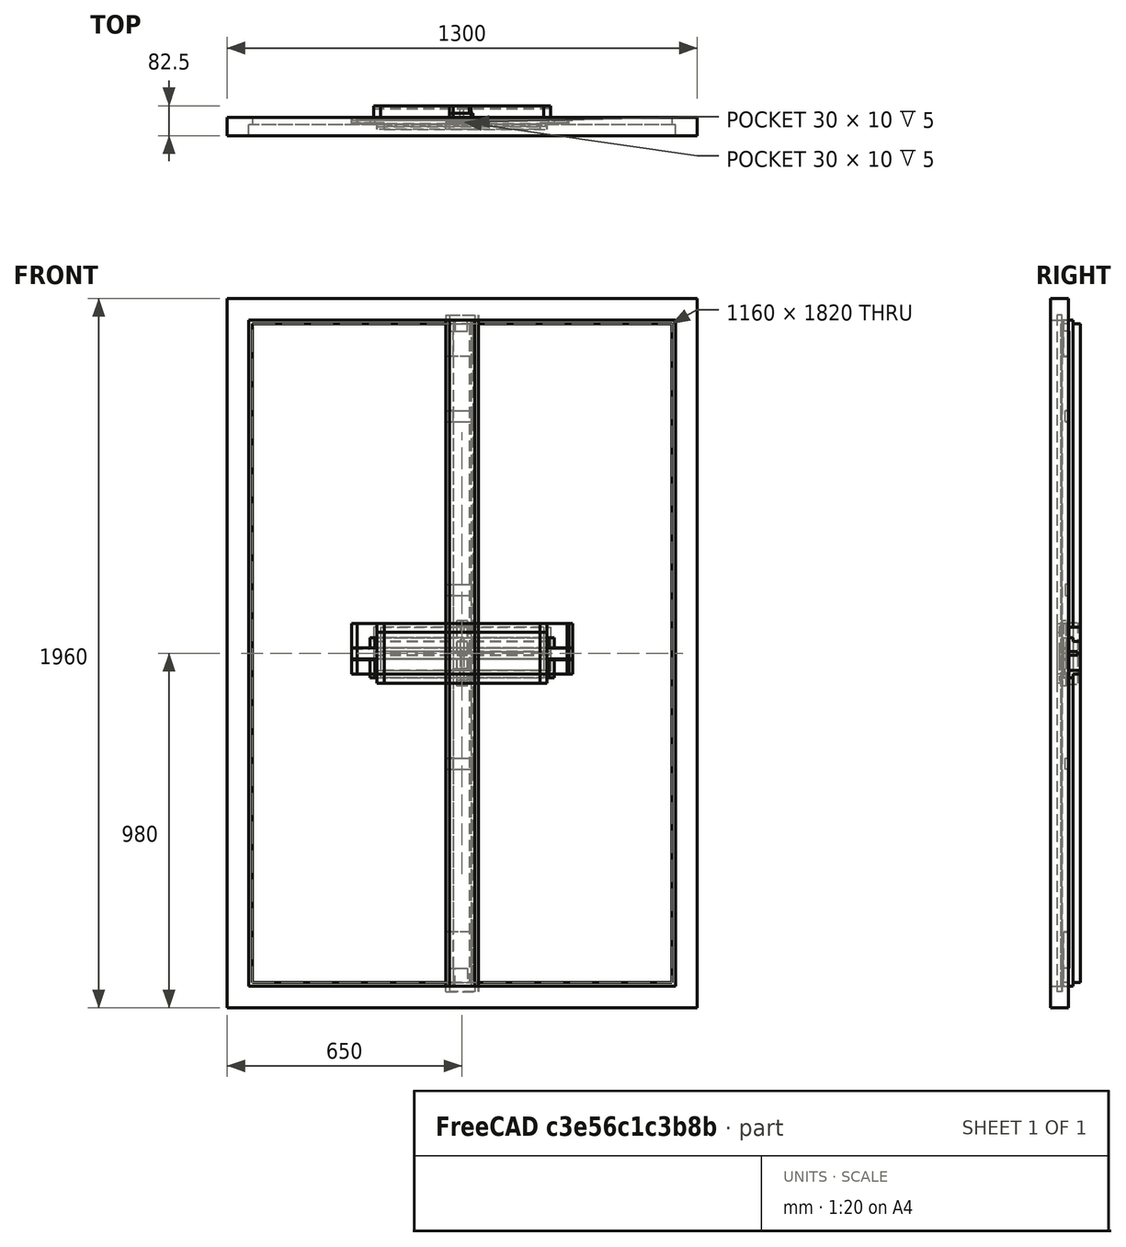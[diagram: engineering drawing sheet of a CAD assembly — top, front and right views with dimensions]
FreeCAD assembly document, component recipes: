
FREECAD ASSEMBLY — COMPONENT RECIPES ("F4.0")

This assembly document has 17 components, labeled P0..P16 below (a component is one placed body or linked part). 17 of them carry a construction recipe — the FreeCAD feature program that regenerates the part from scratch, quoted from this document or its linked companion documents; the rest are supplied as boundary geometry only. No exploded tour is included for this assembly.
COMPONENT P0 — recipe-attached ("Frame002", modeled in this document).
Construction recipe (the document's own serialized feature program — sketch geometry with constraints, then the solid features built on it; lengths are millimeters unless a unit is written):

FEATURE [Sketcher::SketchObject] Sketch064  label="FrameSketch"
  ArcFitTolerance = 0
  AttachmentSupport = -> [XZ_Plane013]
  FullyConstrained = true
  MakeInternals = false
  MapMode = 5
  Placement = pos=(0,0,0) rot=(1,0,0;1.5708rad)
  expr: .Constraints.OpeningHeigth = <<Parameters>>.StileLength - <<Parameters>>.WindowFrameRebateDepth * 2
  expr: .Constraints.OpeningWidth = <<Parameters>>.RailLength * 2 - <<Parameters>>.WindowFrameRebateDepth * 2 - <<Parameters>>.IntersectionRebateDepth
  expr: Constraints[22] = .Constraints.OpeningHeigth + 70 mm * 2
  expr: Constraints[23] = .Constraints.OpeningWidth + 70 mm * 2
  sketch-geometry (10):
    g0: LineSegment StartX=-650 StartY=980 StartZ=0 EndX=-650 EndY=-980 EndZ=0
    g1: LineSegment StartX=-650 StartY=-980 StartZ=0 EndX=650 EndY=-980 EndZ=0
    g2: LineSegment StartX=650 StartY=-980 StartZ=0 EndX=650 EndY=980 EndZ=0
    g3: LineSegment StartX=650 StartY=980 StartZ=0 EndX=-650 EndY=980 EndZ=0
    g4: GeomPoint [constr] X=2.96e-14 Y=2.2e-15 Z=0
    g5: LineSegment StartX=-580 StartY=910 StartZ=0 EndX=-580 EndY=-910 EndZ=0
    g6: LineSegment StartX=-580 StartY=-910 StartZ=0 EndX=580 EndY=-910 EndZ=0
    g7: LineSegment StartX=580 StartY=-910 StartZ=0 EndX=580 EndY=910 EndZ=0
    g8: LineSegment StartX=580 StartY=910 StartZ=0 EndX=-580 EndY=910 EndZ=0
    g9: GeomPoint [constr] X=2.96e-14 Y=2.2e-15 Z=0
  constraints (24):
    c: Coincident(g0,g1)
    c: Coincident(g1,g2)
    c: Coincident(g2,g3)
    c: Coincident(g3,g0)
    c: Vertical(g0)
    c: Vertical(g2)
    c: Horizontal(g1)
    c: Horizontal(g3)
    c: Symmetric(g2,g0,g4)
    c: Coincident(g4,g-1)
    c: Coincident(g5,g6)
    c: Coincident(g6,g7)
    c: Coincident(g7,g8)
    c: Coincident(g8,g5)
    c: Vertical(g5)
    c: Vertical(g7)
    c: Horizontal(g6)
    c: Horizontal(g8)
    c: Symmetric(g7,g5,g9)
    c: Coincident(g9,g4)
    c: DistanceY(g5,g5) = 1820  'OpeningHeigth'
    c: DistanceX(g6,g6) = 1160  'OpeningWidth'
    c: DistanceY(g0,g0) = 1960
    c: DistanceX(g1,g1) = 1300
FEATURE [PartDesign::Pad] Pad006  label="Frame001"
  Direction = (0,-1,2e-16)
  Length = 50
  Length2 = 10
  Placement = pos=(0,0,0) rot=(1,0,0;1.5708rad)
  Profile = -> Sketch064
  ReferenceAxis = -> Sketch064 [N_Axis]
  Refine = true
  Suppressed = false
  Type = 0
  expr: Length = <<Parameters>>.FrameThickness
FEATURE [Sketcher::SketchObject] Sketch065
  ArcFitTolerance = 0
  AttachmentSupport = -> [Pad006]
  FullyConstrained = true
  MakeInternals = false
  MapMode = 5
  Placement = pos=(0,-50,0) rot=(1,0,0;1.5708rad)
  expr: Constraints[10] = <<FrameSketch>>.Constraints.OpeningWidth + 2 * <<Parameters>>.IntersectionRebateDepth
  expr: Constraints[11] = <<FrameSketch>>.Constraints.OpeningHeigth + 2 * <<Parameters>>.IntersectionRebateDepth
  sketch-geometry (5):
    g0: LineSegment StartX=-590 StartY=920 StartZ=0 EndX=-590 EndY=-920 EndZ=0
    g1: LineSegment StartX=-590 StartY=-920 StartZ=0 EndX=590 EndY=-920 EndZ=0
    g2: LineSegment StartX=590 StartY=-920 StartZ=0 EndX=590 EndY=920 EndZ=0
    g3: LineSegment StartX=590 StartY=920 StartZ=0 EndX=-590 EndY=920 EndZ=0
    g4: GeomPoint [constr] X=0 Y=0 Z=0
  constraints (12):
    c: Coincident(g0,g1)
    c: Coincident(g1,g2)
    c: Coincident(g2,g3)
    c: Coincident(g3,g0)
    c: Vertical(g0)
    c: Vertical(g2)
    c: Horizontal(g1)
    c: Horizontal(g3)
    c: Symmetric(g2,g0,g4)
    c: Coincident(g4,g-1)
    c: DistanceX(g3,g3) = 1180
    c: DistanceY(g0,g0) = 1840
FEATURE [PartDesign::Pocket] Pocket057
  BaseFeature = -> Pad006
  Direction = (0,1,-2e-16)
  Length = 30
  Length2 = 5
  Placement = pos=(0,0,0) rot=(1,0,0;1.5708rad)
  Profile = -> Sketch065
  ReferenceAxis = -> Sketch065 [N_Axis]
  Refine = true
  Suppressed = false
  Type = 0
  expr: Length = <<Parameters>>.FrameThickness - <<Parameters>>.WindowFrameRebateWidth
FEATURE [PartDesign::Body] Body013  label="Frame"
  AllowCompound = false
  Group = -> [Sketch064,Pad006,Sketch065,Pocket057]
  Origin = -> Origin013
  Tip = -> Pocket057
COMPONENT P1 — recipe-attached ("Muntin bar001", modeled in this document).
Construction recipe (the document's own serialized feature program — sketch geometry with constraints, then the solid features built on it; lengths are millimeters unless a unit is written):

FEATURE [PartDesign::Plane] DatumPlane  label="DatumPlane top"
  AttachmentOffset = pos=(0,0,90) rot=(0,0,1;0rad)
  AttachmentSupport = -> [X_Axis]
  Length = 30
  MapMode = 2
  Placement = pos=(0,0,90) rot=(0,0,1;0rad)
  ResizeMode = 1
  Width = 50
  expr: .AttachmentOffset.Base.z = <<Parameters>>.MuntinBarLength / 2
  expr: Length = <<Parameters>>.MuntinWidth
  expr: Width = <<Parameters>>.MuntinThickness
FEATURE [PartDesign::Plane] DatumPlane001  label="DatumPlane right"
  AttachmentOffset = pos=(0,0,15) rot=(0,0,1;0rad)
  AttachmentSupport = -> [X_Axis]
  Length = 50
  MapMode = 4
  Placement = pos=(15,0,0) rot=(0.57735,0.57735,0.57735;2.0944rad)
  ResizeMode = 1
  Width = 180
  expr: .AttachmentOffset.Base.z = <<Parameters>>.MuntinWidth / 2
  expr: Length = <<Parameters>>.MuntinThickness
  expr: Width = <<Parameters>>.MuntinBarLength
FEATURE [PartDesign::Plane] DatumPlane002  label="DatumPlane front"
  AttachmentOffset = pos=(0,0,25) rot=(0,0,1;0rad)
  AttachmentSupport = -> [X_Axis]
  Length = 30
  MapMode = 3
  Placement = pos=(0,-25,5.6e-15) rot=(1,0,0;1.5708rad)
  ResizeMode = 1
  Width = 180
  expr: .AttachmentOffset.Base.z = <<Parameters>>.MuntinThickness / 2
  expr: Length = <<Parameters>>.MuntinWidth
  expr: Width = <<Parameters>>.MuntinBarLength
FEATURE [Sketcher::SketchObject] Sketch
  ArcFitTolerance = 0
  AttachmentSupport = -> [DatumPlane]
  FullyConstrained = true
  MakeInternals = false
  MapMode = 5
  Placement = pos=(0,0,90) rot=(0,0,1;0rad)
  expr: Constraints[10] = <<Parameters>>.MuntinWidth
  expr: Constraints[11] = <<Parameters>>.MuntinThickness
  sketch-geometry (5):
    g0: LineSegment StartX=-15 StartY=25 StartZ=0 EndX=-15 EndY=-25 EndZ=0
    g1: LineSegment StartX=-15 StartY=-25 StartZ=0 EndX=15 EndY=-25 EndZ=0
    g2: LineSegment StartX=15 StartY=-25 StartZ=0 EndX=15 EndY=25 EndZ=0
    g3: LineSegment StartX=15 StartY=25 StartZ=0 EndX=-15 EndY=25 EndZ=0
    g4: GeomPoint [constr] X=0 Y=0 Z=0
  constraints (12):
    c: Coincident(g0,g1)
    c: Coincident(g1,g2)
    c: Coincident(g2,g3)
    c: Coincident(g3,g0)
    c: Vertical(g0)
    c: Vertical(g2)
    c: Horizontal(g1)
    c: Horizontal(g3)
    c: Symmetric(g2,g0,g4)
    c: Coincident(g4,g-1)
    c: DistanceX(g3,g3) = 30
    c: DistanceY(g0,g0) = 50
FEATURE [PartDesign::Pad] Pad  label="Stock"
  Direction = (0,0,1)
  Length = 180
  Length2 = 10
  Placement = pos=(0,0,90) rot=(0,0,1;0rad)
  Profile = -> Sketch
  ReferenceAxis = -> Sketch [N_Axis]
  Refine = true
  Reversed = true
  Suppressed = false
  Type = 0
  expr: Length = <<Parameters>>.MuntinBarLength
FEATURE [Sketcher::SketchObject] Sketch001
  ArcFitTolerance = 0
  AttachmentSupport = -> [DatumPlane001]
  ExternalGeometry = -> [DatumPlane,DatumPlane002]
  FullyConstrained = true
  MakeInternals = false
  MapMode = 5
  Placement = pos=(15,0,0) rot=(0.57735,0.57735,0.57735;2.0944rad)
  expr: Constraints[14] = <<Parameters>>.MuntinBarTenonLength
  expr: Constraints[16] = <<Parameters>>.GlassRebateDepth
  expr: Constraints[18] = <<Parameters>>.MuntinThickness
  expr: Constraints[19] = <<Parameters>>.MuntinTenonThickness
  expr: Constraints[20] = <<Parameters>>.MuntinBarTenonLength - <<Parameters>>.GlassRebateWidth
  sketch-geometry (8):
    g0: LineSegment StartX=-17 StartY=90 StartZ=0 EndX=-17 EndY=75 EndZ=0
    g1: LineSegment StartX=-17 StartY=75 StartZ=0 EndX=-25 EndY=75 EndZ=0
    g2: LineSegment StartX=-25 StartY=75 StartZ=0 EndX=-25 EndY=90 EndZ=0
    g3: LineSegment StartX=-25 StartY=90 StartZ=0 EndX=-17 EndY=90 EndZ=0
    g4: LineSegment StartX=-7 StartY=90 StartZ=0 EndX=-7 EndY=85 EndZ=0
    g5: LineSegment StartX=-7 StartY=85 StartZ=0 EndX=25 EndY=85 EndZ=0
    g6: LineSegment StartX=25 StartY=85 StartZ=0 EndX=25 EndY=90 EndZ=0
    g7: LineSegment StartX=25 StartY=90 StartZ=0 EndX=-7 EndY=90 EndZ=0
  constraints (23):
    c: Coincident(g0,g1)
    c: Coincident(g1,g2)
    c: Coincident(g2,g3)
    c: Coincident(g3,g0)
    c: Vertical(g0)
    c: Horizontal(g1)
    c: Coincident(g4,g5)
    c: Coincident(g5,g6)
    c: Coincident(g6,g7)
    c: Coincident(g7,g4)
    c: Vertical(g4)
    c: Vertical(g6)
    c: Horizontal(g5)
    c: Horizontal(g7)
    c: DistanceY(g0,g0) = 15
    c: DistanceX(g1,g1) = -8
    c: DistanceX(g7,g7) = 32
    c: Horizontal(g4,g2)
    c: DistanceX(g2,g6) = 50
    c: DistanceX(g0,g4) = 10
    c: DistanceY(g6,g6) = 5
    c: Tangent(g2,g-4)
    c: Tangent(g3,g-3)
FEATURE [PartDesign::Pocket] Pocket  label="Tenon top"
  BaseFeature = -> Pad
  Direction = (-1,0,0)
  Length = 5
  Length2 = 5
  Placement = pos=(0,0,90) rot=(0,0,1;0rad)
  Profile = -> Sketch001
  ReferenceAxis = -> Sketch001 [N_Axis]
  Refine = true
  Suppressed = false
  Type = 1
FEATURE [PartDesign::Mirrored] Mirrored  label="Tenon bottom"
  BaseFeature = -> Pocket
  MirrorPlane = -> XY_Plane
  Originals = -> [Pocket]
  Placement = pos=(0,0,90) rot=(0,0,1;0rad)
  Refine = true
  Suppressed = false
  TransformMode = 0
FEATURE [Sketcher::SketchObject] Sketch002
  ArcFitTolerance = 0
  AttachmentSupport = -> [DatumPlane]
  ExternalGeometry = -> [DatumPlane001,DatumPlane002]
  FullyConstrained = true
  MakeInternals = false
  MapMode = 5
  Placement = pos=(0,0,90) rot=(0,0,1;0rad)
  expr: Constraints[7] = <<Parameters>>.GlassRebateDepth
  expr: Constraints[8] = <<Parameters>>.GlassRebateWidth
  expr: Constraints[9] = <<Parameters>>.MuntinThickness
  sketch-geometry (4):
    g0: LineSegment StartX=5 StartY=25 StartZ=0 EndX=5 EndY=-7 EndZ=0
    g1: LineSegment StartX=5 StartY=-7 StartZ=0 EndX=15 EndY=-7 EndZ=0
    g2: LineSegment StartX=15 StartY=-7 StartZ=0 EndX=15 EndY=25 EndZ=0
    g3: LineSegment StartX=15 StartY=25 StartZ=0 EndX=5 EndY=25 EndZ=0
  constraints (11):
    c: Coincident(g0,g1)
    c: Coincident(g1,g2)
    c: Coincident(g2,g3)
    c: Coincident(g3,g0)
    c: Vertical(g0)
    c: Horizontal(g1)
    c: Horizontal(g3)
    c: DistanceY(g0,g0) = 32
    c: DistanceX(g3,g3) = 10
    c: Distance(g2,g-4) = 50
    c: Tangent(g2,g-3)
FEATURE [PartDesign::Pocket] Pocket001  label="Glass rebate right"
  BaseFeature = -> Mirrored
  Direction = (0,0,-1)
  Length = 5
  Length2 = 5
  Placement = pos=(0,0,90) rot=(0,0,1;0rad)
  Profile = -> Sketch002
  ReferenceAxis = -> Sketch002 [N_Axis]
  Refine = true
  Suppressed = false
  Type = 1
FEATURE [PartDesign::Mirrored] Mirrored001  label="Glass rebate left"
  BaseFeature = -> Pocket001
  MirrorPlane = -> Sketch002 [V_Axis]
  Originals = -> [Pocket001]
  Placement = pos=(0,0,90) rot=(0,0,1;0rad)
  Refine = true
  Suppressed = false
  TransformMode = 0
FEATURE [PartDesign::Body] Body  label="Muntin bar"
  AllowCompound = false
  Group = -> [DatumPlane,DatumPlane001,DatumPlane002,Sketch,Pad,Sketch001,Pocket,Mirrored,Sketch002,Pocket001,Mirrored001]
  Origin = -> Origin
  Tip = -> Mirrored001
COMPONENT P2 — same part as P1; its construction recipe is shown at P1.
COMPONENT P3 — recipe-attached ("Muntin partitioned left001", modeled in this document).
Construction recipe (the document's own serialized feature program — sketch geometry with constraints, then the solid features built on it; lengths are millimeters unless a unit is written):

FEATURE [PartDesign::FeatureBase] BaseFeature002
  BaseFeature = -> Binder002
  Suppressed = false
FEATURE [PartDesign::Plane] DatumPlane023  label="DatumPlane top005"
  AttachmentOffset = pos=(0,0,15) rot=(0,0,1;0rad)
  AttachmentSupport = -> [X_Axis006]
  Length = 610
  MapMode = 2
  Placement = pos=(0,0,15) rot=(0,0,1;0rad)
  ResizeMode = 1
  Width = 50
  expr: .AttachmentOffset.Base.z = <<Parameters>>.MuntinWidth / 2
  expr: Length = <<Parameters>>.RailLength
  expr: Width = <<Parameters>>.MuntinThickness
FEATURE [PartDesign::Plane] DatumPlane024  label="DatumPlane right004"
  AttachmentOffset = pos=(0,0,305) rot=(0,0,1;0rad)
  AttachmentSupport = -> [X_Axis006]
  Length = 50
  MapMode = 4
  Placement = pos=(305,0,0) rot=(0.57735,0.57735,0.57735;2.0944rad)
  ResizeMode = 1
  Width = 30
  expr: .AttachmentOffset.Base.z = <<Parameters>>.RailLength / 2
  expr: Length = <<Parameters>>.MuntinThickness
  expr: Width = <<Parameters>>.MuntinWidth
FEATURE [PartDesign::Plane] DatumPlane025  label="DatumPlane front003"
  AttachmentOffset = pos=(0,0,25) rot=(0,0,1;0rad)
  AttachmentSupport = -> [X_Axis006]
  Length = 610
  MapMode = 3
  Placement = pos=(0,-25,5.6e-15) rot=(1,0,0;1.5708rad)
  ResizeMode = 1
  Width = 30
  expr: .AttachmentOffset.Base.z = <<Parameters>>.MuntinThickness / 2
  expr: Length = <<Parameters>>.RailLength
  expr: Width = <<Parameters>>.MuntinWidth
FEATURE [PartDesign::Plane] DatumPlane026  label="DatumPlane left004"
  AttachmentOffset = pos=(0,0,305) rot=(0,0,1;0rad)
  AttachmentSupport = -> [X_Axis006]
  Length = 50
  MapMode = 4
  Placement = pos=(-305,0,0) rot=(0.57735,-0.57735,-0.57735;2.0944rad)
  ResizeMode = 1
  Width = 30
  expr: .AttachmentOffset.Base.z = <<Parameters>>.RailLength / 2
  expr: Length = <<Parameters>>.MuntinThickness
  expr: Width = <<Parameters>>.MuntinWidth
FEATURE [PartDesign::Plane] DatumPlane027  label="DatumPlane rear004"
  AttachmentOffset = pos=(0,0,25) rot=(0,0,1;0rad)
  AttachmentSupport = -> [X_Axis006]
  Length = 610
  MapMode = 3
  Placement = pos=(0,25,-5.6e-15) rot=(0,0.707107,0.707107;3.14159rad)
  ResizeMode = 1
  Width = 30
  expr: .AttachmentOffset.Base.z = <<Parameters>>.MuntinThickness / 2
  expr: Length = <<Parameters>>.RailLength
  expr: Width = <<Parameters>>.MuntinWidth
FEATURE [Sketcher::SketchObject] Sketch040
  ArcFitTolerance = 0
  AttachmentSupport = -> [DatumPlane023]
  ExternalGeometry = -> [DatumPlane027,DatumPlane024]
  FullyConstrained = true
  MakeInternals = false
  MapMode = 5
  Placement = pos=(0,0,15) rot=(0,0,1;0rad)
  expr: Constraints[10] = <<Parameters>>.GlassRebateDepth
  expr: Constraints[11] = <<Parameters>>.GlassOpeningWidth / 2 - <<Parameters>>.MuntinWidth / 2 + <<Parameters>>.StileInnerWidth
  expr: Constraints[8] = <<Parameters>>.MuntinTenonThickness
  expr: Constraints[9] = <<Parameters>>.MuntinWidth
  sketch-geometry (4):
    g0: LineSegment StartX=-5 StartY=-7 StartZ=0 EndX=-5 EndY=-17 EndZ=0
    g1: LineSegment StartX=-5 StartY=-17 StartZ=0 EndX=25 EndY=-17 EndZ=0
    g2: LineSegment StartX=25 StartY=-17 StartZ=0 EndX=25 EndY=-7 EndZ=0
    g3: LineSegment StartX=25 StartY=-7 StartZ=0 EndX=-5 EndY=-7 EndZ=0
  constraints (12):
    c: Coincident(g0,g1)
    c: Coincident(g1,g2)
    c: Coincident(g2,g3)
    c: Coincident(g3,g0)
    c: Vertical(g0)
    c: Vertical(g2)
    c: Horizontal(g1)
    c: Horizontal(g3)
    c: DistanceY(g2,g2) = 10
    c: DistanceX(g1,g1) = 30
    c: Distance(g0,g-3) = 32
    c: Distance(g2,g-4) = 280
FEATURE [PartDesign::Pocket] Pocket035  label="Muntin bar mortise"
  BaseFeature = -> BaseFeature002
  Direction = (0,0,-1)
  Length = 15
  Length2 = 5
  Profile = -> Sketch040
  ReferenceAxis = -> Sketch040 [N_Axis]
  Refine = true
  Suppressed = false
  Type = 0
  expr: Length = <<Parameters>>.MuntinBarTenonLength
FEATURE [Sketcher::SketchObject] Sketch041
  ArcFitTolerance = 0
  AttachmentSupport = -> [DatumPlane023]
  ExternalGeometry = -> [DatumPlane024,DatumPlane027]
  FullyConstrained = true
  MakeInternals = false
  MapMode = 5
  Placement = pos=(0,0,15) rot=(0,0,1;0rad)
  expr: Constraints[10] = <<Parameters>>.IntersectionRebateWidth
  expr: Constraints[5] = <<Parameters>>.IntersectionRebateDepth
  expr: Constraints[6] = <<Parameters>>.IntersectionRebateWidth
  sketch-geometry (4):
    g0: LineSegment StartX=295 StartY=-7.5 StartZ=0 EndX=295 EndY=-40 EndZ=0
    g1: LineSegment StartX=295 StartY=-40 StartZ=0 EndX=305 EndY=-40 EndZ=0
    g2: LineSegment StartX=305 StartY=-40 StartZ=0 EndX=305 EndY=-7.5 EndZ=0
    g3: LineSegment StartX=305 StartY=-7.5 StartZ=0 EndX=295 EndY=-7.5 EndZ=0
  constraints (11):
    c: Coincident(g0,g1)
    c: Coincident(g1,g2)
    c: Coincident(g2,g3)
    c: Coincident(g3,g0)
    c: Horizontal(g3)
    c: Distance(g3,g3) = 10
    c: DistanceY(g0,g0) = 32.5
    c: Vertical(g0,g0)
    c: Horizontal(g0,g1)
    c: Tangent(g2,g-3)
    c: Distance(g2,g-4) = 32.5
FEATURE [PartDesign::Pocket] Pocket036  label="Frame inner intersection rebate001"
  BaseFeature = -> Pocket035
  Direction = (0,0,-1)
  Length = 5
  Length2 = 5
  Profile = -> Sketch041
  ReferenceAxis = -> Sketch041 [N_Axis]
  Refine = true
  Suppressed = false
  Type = 1
FEATURE [PartDesign::Body] Body006  label="Muntin partitioned left"
  AllowCompound = false
  Group = -> [DatumPlane023,DatumPlane024,DatumPlane025,DatumPlane026,DatumPlane027,BaseFeature002,Sketch040,Pocket035,Sketch041,Pocket036]
  Origin = -> Origin006
  Tip = -> Pocket036
COMPONENT P4 — recipe-attached ("Muntin partitioned right001", modeled in this document).
Construction recipe (the document's own serialized feature program — sketch geometry with constraints, then the solid features built on it; lengths are millimeters unless a unit is written):

FEATURE [PartDesign::FeatureBase] BaseFeature004
  BaseFeature = -> Part__Mirroring003
  Suppressed = false
FEATURE [PartDesign::Body] Body008  label="Muntin partitioned right"
  AllowCompound = false
  BaseFeature = -> Part__Mirroring003
  Group = -> [BaseFeature004]
  Origin = -> Origin008
  Tip = -> BaseFeature004
COMPONENT P5 — recipe-attached ("Muntin single left001", modeled in this document).
Construction recipe (the document's own serialized feature program — sketch geometry with constraints, then the solid features built on it; lengths are millimeters unless a unit is written):

FEATURE [PartDesign::Plane] DatumPlane018  label="DatumPlane top004"
  AttachmentOffset = pos=(0,0,15) rot=(0,0,1;0rad)
  AttachmentSupport = -> [X_Axis005]
  Length = 610
  MapMode = 2
  Placement = pos=(0,0,15) rot=(0,0,1;0rad)
  ResizeMode = 1
  Width = 50
  expr: .AttachmentOffset.Base.z = <<Parameters>>.MuntinWidth / 2
  expr: Length = <<Parameters>>.RailLength
  expr: Width = <<Parameters>>.MuntinThickness
FEATURE [PartDesign::Plane] DatumPlane019  label="DatumPlane right003"
  AttachmentOffset = pos=(0,0,305) rot=(0,0,1;0rad)
  AttachmentSupport = -> [X_Axis005]
  Length = 50
  MapMode = 4
  Placement = pos=(305,0,0) rot=(0.57735,0.57735,0.57735;2.0944rad)
  ResizeMode = 1
  Width = 30
  expr: .AttachmentOffset.Base.z = <<Parameters>>.RailLength / 2
  expr: Length = <<Parameters>>.MuntinThickness
  expr: Width = <<Parameters>>.MuntinWidth
FEATURE [PartDesign::Plane] DatumPlane020  label="DatumPlane front002"
  AttachmentOffset = pos=(0,0,25) rot=(0,0,1;0rad)
  AttachmentSupport = -> [X_Axis005]
  Length = 610
  MapMode = 3
  Placement = pos=(0,-25,5.6e-15) rot=(1,0,0;1.5708rad)
  ResizeMode = 1
  Width = 30
  expr: .AttachmentOffset.Base.z = <<Parameters>>.MuntinThickness / 2
  expr: Length = <<Parameters>>.RailLength
  expr: Width = <<Parameters>>.MuntinWidth
FEATURE [Sketcher::SketchObject] Sketch033
  ArcFitTolerance = 0
  AttachmentSupport = -> [DatumPlane019]
  FullyConstrained = true
  MakeInternals = false
  MapMode = 5
  Placement = pos=(305,0,0) rot=(0.57735,0.57735,0.57735;2.0944rad)
  expr: Constraints[10] = <<Parameters>>.MuntinThickness
  expr: Constraints[11] = <<Parameters>>.MuntinWidth
  sketch-geometry (5):
    g0: LineSegment StartX=-25 StartY=15 StartZ=0 EndX=-25 EndY=-15 EndZ=0
    g1: LineSegment StartX=-25 StartY=-15 StartZ=0 EndX=25 EndY=-15 EndZ=0
    g2: LineSegment StartX=25 StartY=-15 StartZ=0 EndX=25 EndY=15 EndZ=0
    g3: LineSegment StartX=25 StartY=15 StartZ=0 EndX=-25 EndY=15 EndZ=0
    g4: GeomPoint [constr] X=0 Y=0 Z=0
  constraints (12):
    c: Coincident(g0,g1)
    c: Coincident(g1,g2)
    c: Coincident(g2,g3)
    c: Coincident(g3,g0)
    c: Vertical(g0)
    c: Vertical(g2)
    c: Horizontal(g1)
    c: Horizontal(g3)
    c: Symmetric(g2,g0,g4)
    c: Coincident(g4,g-1)
    c: DistanceX(g3,g3) = 50
    c: DistanceY(g0,g0) = 30
FEATURE [PartDesign::Pad] Pad003  label="Stock003"
  Direction = (1,0,0)
  Length = 610
  Length2 = 10
  Placement = pos=(305,0,0) rot=(0.57735,0.57735,0.57735;2.0944rad)
  Profile = -> Sketch033
  ReferenceAxis = -> Sketch033 [N_Axis]
  Refine = true
  Reversed = true
  Suppressed = false
  Type = 0
  expr: Length = <<Parameters>>.RailLength
FEATURE [Sketcher::SketchObject] Sketch034
  ArcFitTolerance = 0
  AttachmentSupport = -> [DatumPlane018]
  ExternalGeometry = -> [DatumPlane019,DatumPlane020]
  FullyConstrained = true
  MakeInternals = false
  MapMode = 5
  Placement = pos=(0,0,15) rot=(0,0,1;0rad)
  expr: Constraints[14] = <<Parameters>>.StileInnerWidth - <<Parameters>>.GlassRebateWidth
  expr: Constraints[15] = <<Parameters>>.MuntinThickness
  expr: Constraints[16] = <<Parameters>>.GlassRebateDepth
  expr: Constraints[17] = <<Parameters>>.MuntinTenonThickness
  expr: Constraints[18] = <<Parameters>>.StileInnerWidth
  sketch-geometry (8):
    g0: LineSegment StartX=305 StartY=-17 StartZ=0 EndX=235 EndY=-17 EndZ=0
    g1: LineSegment StartX=235 StartY=-17 StartZ=0 EndX=235 EndY=-25 EndZ=0
    g2: LineSegment StartX=235 StartY=-25 StartZ=0 EndX=305 EndY=-25 EndZ=0
    g3: LineSegment StartX=305 StartY=-25 StartZ=0 EndX=305 EndY=-17 EndZ=0
    g4: LineSegment StartX=305 StartY=25 StartZ=0 EndX=245 EndY=25 EndZ=0
    g5: LineSegment StartX=245 StartY=25 StartZ=0 EndX=245 EndY=-7 EndZ=0
    g6: LineSegment StartX=245 StartY=-7 StartZ=0 EndX=305 EndY=-7 EndZ=0
    g7: LineSegment StartX=305 StartY=-7 StartZ=0 EndX=305 EndY=25 EndZ=0
  constraints (22):
    c: Coincident(g0,g1)
    c: Coincident(g1,g2)
    c: Coincident(g2,g3)
    c: Coincident(g3,g0)
    c: Horizontal(g0)
    c: Vertical(g1)
    c: Vertical(g3)
    c: Coincident(g4,g5)
    c: Coincident(g5,g6)
    c: Coincident(g6,g7)
    c: Coincident(g7,g4)
    c: Horizontal(g4)
    c: Horizontal(g6)
    c: Vertical(g5)
    c: DistanceX(g4,g4) = 60
    c: DistanceY(g2,g4) = 50
    c: DistanceY(g7,g7) = 32
    c: DistanceY(g0,g6) = 10
    c: Distance(g2,g2) = 70
    c: Tangent(g7,g-3)
    c: Vertical(g0,g6)
    c: Tangent(g2,g-4)
FEATURE [PartDesign::Pocket] Pocket029  label="Tenon inner"
  BaseFeature = -> Pad003
  Direction = (0,0,-1)
  Length = 5
  Length2 = 5
  Placement = pos=(305,0,0) rot=(0.57735,0.57735,0.57735;2.0944rad)
  Profile = -> Sketch034
  ReferenceAxis = -> Sketch034 [N_Axis]
  Refine = true
  Suppressed = false
  Type = 1
FEATURE [PartDesign::Plane] DatumPlane021  label="DatumPlane left003"
  AttachmentOffset = pos=(0,0,305) rot=(0,0,1;0rad)
  AttachmentSupport = -> [X_Axis005]
  Length = 50
  MapMode = 4
  Placement = pos=(-305,0,0) rot=(0.57735,-0.57735,-0.57735;2.0944rad)
  ResizeMode = 1
  Width = 30
  expr: .AttachmentOffset.Base.z = <<Parameters>>.RailLength / 2
  expr: Length = <<Parameters>>.MuntinThickness
  expr: Width = <<Parameters>>.MuntinWidth
FEATURE [Sketcher::SketchObject] Sketch036
  ArcFitTolerance = 0
  AttachmentSupport = -> [DatumPlane018]
  ExternalGeometry = -> [DatumPlane021,DatumPlane020]
  FullyConstrained = true
  MakeInternals = false
  MapMode = 5
  Placement = pos=(0,0,15) rot=(0,0,1;0rad)
  expr: Constraints[14] = <<Parameters>>.StileOuterWidth
  expr: Constraints[16] = <<Parameters>>.StileOuterWidth - <<Parameters>>.GlassRebateWidth
  expr: Constraints[17] = <<Parameters>>.GlassRebateDepth
  expr: Constraints[18] = <<Parameters>>.MuntinTenonThickness
  expr: Constraints[19] = <<Parameters>>.MuntinThickness
  sketch-geometry (8):
    g0: LineSegment StartX=-305 StartY=25 StartZ=0 EndX=-305 EndY=-7 EndZ=0
    g1: LineSegment StartX=-305 StartY=-7 StartZ=0 EndX=-225 EndY=-7 EndZ=0
    g2: LineSegment StartX=-225 StartY=-7 StartZ=0 EndX=-225 EndY=25 EndZ=0
    g3: LineSegment StartX=-225 StartY=25 StartZ=0 EndX=-305 EndY=25 EndZ=0
    g4: LineSegment StartX=-305 StartY=-17 StartZ=0 EndX=-305 EndY=-25 EndZ=0
    g5: LineSegment StartX=-305 StartY=-25 StartZ=0 EndX=-215 EndY=-25 EndZ=0
    g6: LineSegment StartX=-215 StartY=-25 StartZ=0 EndX=-215 EndY=-17 EndZ=0
    g7: LineSegment StartX=-215 StartY=-17 StartZ=0 EndX=-305 EndY=-17 EndZ=0
  constraints (22):
    c: Coincident(g0,g1)
    c: Coincident(g1,g2)
    c: Coincident(g2,g3)
    c: Coincident(g3,g0)
    c: Vertical(g2)
    c: Horizontal(g1)
    c: Horizontal(g3)
    c: Coincident(g4,g5)
    c: Coincident(g5,g6)
    c: Coincident(g6,g7)
    c: Coincident(g7,g4)
    c: Vertical(g4)
    c: Vertical(g6)
    c: Horizontal(g7)
    c: DistanceX(g5,g5) = 90
    c: Vertical(g4,g0)
    c: DistanceX(g3,g3) = 80
    c: DistanceY(g0,g0) = 32
    c: Distance(g0,g4) = 10
    c: DistanceY(g4,g0) = 50
    c: Tangent(g0,g-3)
    c: Tangent(g5,g-4)
FEATURE [PartDesign::Pocket] Pocket031  label="Tenon outer"
  BaseFeature = -> Pocket029
  Direction = (0,0,-1)
  Length = 5
  Length2 = 5
  Placement = pos=(305,0,0) rot=(0.57735,0.57735,0.57735;2.0944rad)
  Profile = -> Sketch036
  ReferenceAxis = -> Sketch036 [N_Axis]
  Refine = true
  Suppressed = false
  Type = 1
FEATURE [PartDesign::Plane] DatumPlane022  label="DatumPlane rear003"
  AttachmentOffset = pos=(0,0,25) rot=(0,0,1;0rad)
  AttachmentSupport = -> [X_Axis005]
  Length = 610
  MapMode = 3
  Placement = pos=(0,25,-5.6e-15) rot=(0,0.707107,0.707107;3.14159rad)
  ResizeMode = 1
  Width = 30
  expr: .AttachmentOffset.Base.z = <<Parameters>>.MuntinThickness / 2
  expr: Length = <<Parameters>>.RailLength
  expr: Width = <<Parameters>>.MuntinWidth
FEATURE [Sketcher::SketchObject] Sketch037
  ArcFitTolerance = 0
  AttachmentSupport = -> [DatumPlane019]
  ExternalGeometry = -> [DatumPlane018,DatumPlane022]
  FullyConstrained = true
  MakeInternals = false
  MapMode = 5
  Placement = pos=(305,0,0) rot=(0.57735,0.57735,0.57735;2.0944rad)
  expr: Constraints[6] = <<Parameters>>.GlassRebateDepth
  expr: Constraints[7] = <<Parameters>>.GlassRebateWidth
  sketch-geometry (4):
    g0: LineSegment StartX=25 StartY=15 StartZ=0 EndX=-7 EndY=15 EndZ=0
    g1: LineSegment StartX=-7 StartY=15 StartZ=0 EndX=-7 EndY=5 EndZ=0
    g2: LineSegment StartX=-7 StartY=5 StartZ=0 EndX=25 EndY=5 EndZ=0
    g3: LineSegment StartX=25 StartY=5 StartZ=0 EndX=25 EndY=15 EndZ=0
  constraints (10):
    c: Coincident(g0,g1)
    c: Coincident(g1,g2)
    c: Coincident(g2,g3)
    c: Coincident(g3,g0)
    c: Horizontal(g2)
    c: Vertical(g1)
    c: DistanceX(g0,g0) = 32
    c: DistanceY(g3,g3) = 10
    c: Tangent(g-4,g3)
    c: Tangent(g0,g-3)
FEATURE [PartDesign::Pocket] Pocket032  label="Glass rebate top"
  BaseFeature = -> Pocket031
  Direction = (-1,0,0)
  Length = 5
  Length2 = 5
  Placement = pos=(305,0,0) rot=(0.57735,0.57735,0.57735;2.0944rad)
  Profile = -> Sketch037
  ReferenceAxis = -> Sketch037 [N_Axis]
  Refine = true
  Suppressed = false
  Type = 1
FEATURE [PartDesign::Mirrored] Mirrored004  label="Glass rebate bottom"
  BaseFeature = -> Pocket032
  MirrorPlane = -> Sketch037 [H_Axis]
  Originals = -> [Pocket032]
  Placement = pos=(305,0,0) rot=(0.57735,0.57735,0.57735;2.0944rad)
  Refine = true
  Suppressed = false
  TransformMode = 0
FEATURE [Sketcher::SketchObject] Sketch038
  ArcFitTolerance = 0
  AttachmentSupport = -> [DatumPlane018]
  ExternalGeometry = -> [DatumPlane021,DatumPlane020]
  FullyConstrained = true
  MakeInternals = false
  MapMode = 5
  Placement = pos=(0,0,15) rot=(0,0,1;0rad)
  expr: Constraints[6] = <<Parameters>>.WindowInnerLipWidth
  expr: Constraints[7] = <<Parameters>>.MuntinThickness
  sketch-geometry (4):
    g0: LineSegment StartX=-305 StartY=25 StartZ=0 EndX=-305 EndY=-25 EndZ=0
    g1: LineSegment StartX=-305 StartY=-25 StartZ=0 EndX=-290 EndY=-25 EndZ=0
    g2: LineSegment StartX=-290 StartY=-25 StartZ=0 EndX=-290 EndY=25 EndZ=0
    g3: LineSegment StartX=-290 StartY=25 StartZ=0 EndX=-305 EndY=25 EndZ=0
  constraints (10):
    c: Coincident(g0,g1)
    c: Coincident(g1,g2)
    c: Coincident(g2,g3)
    c: Coincident(g3,g0)
    c: Vertical(g2)
    c: Horizontal(g3)
    c: Distance(g3,g3) = 15
    c: DistanceY(g0,g0) = 50
    c: Tangent(g0,g-3)
    c: Tangent(g1,g-4)
FEATURE [Sketcher::SketchObject] Sketch039
  ArcFitTolerance = 0
  AttachmentSupport = -> [DatumPlane018]
  ExternalGeometry = -> [DatumPlane019,DatumPlane022]
  FullyConstrained = true
  MakeInternals = false
  MapMode = 5
  Placement = pos=(0,0,15) rot=(0,0,1;0rad)
  expr: Constraints[10] = <<Parameters>>.IntersectionRebateWidth
  expr: Constraints[5] = <<Parameters>>.IntersectionRebateDepth
  expr: Constraints[6] = <<Parameters>>.IntersectionRebateWidth
  sketch-geometry (4):
    g0: LineSegment StartX=295 StartY=-7.5 StartZ=0 EndX=295 EndY=-40 EndZ=0
    g1: LineSegment StartX=295 StartY=-40 StartZ=0 EndX=305 EndY=-40 EndZ=0
    g2: LineSegment StartX=305 StartY=-40 StartZ=0 EndX=305 EndY=-7.5 EndZ=0
    g3: LineSegment StartX=305 StartY=-7.5 StartZ=0 EndX=295 EndY=-7.5 EndZ=0
  constraints (11):
    c: Coincident(g0,g1)
    c: Coincident(g1,g2)
    c: Coincident(g2,g3)
    c: Coincident(g3,g0)
    c: Horizontal(g3)
    c: Distance(g3,g3) = 10
    c: DistanceY(g0,g0) = 32.5
    c: Vertical(g0,g0)
    c: Tangent(g2,g-3)
    c: Horizontal(g0,g1)
    c: Distance(g2,g-4) = 32.5
FEATURE [PartDesign::Pocket] Pocket033  label="Frame outer rebate"
  BaseFeature = -> Mirrored004
  Direction = (0,0,-1)
  Length = 5
  Length2 = 5
  Placement = pos=(305,0,0) rot=(0.57735,0.57735,0.57735;2.0944rad)
  Profile = -> Sketch038
  ReferenceAxis = -> Sketch038 [N_Axis]
  Refine = true
  Suppressed = false
  Type = 1
FEATURE [PartDesign::Pocket] Pocket034  label="Frame inner intersection rebate"
  BaseFeature = -> Pocket033
  Direction = (0,0,-1)
  Length = 5
  Length2 = 5
  Placement = pos=(305,0,0) rot=(0.57735,0.57735,0.57735;2.0944rad)
  Profile = -> Sketch039
  ReferenceAxis = -> Sketch039 [N_Axis]
  Refine = true
  Suppressed = false
  Type = 1
FEATURE [PartDesign::Body] Body005  label="Muntin single left"
  AllowCompound = false
  Group = -> [DatumPlane018,DatumPlane019,DatumPlane020,DatumPlane021,DatumPlane022,Sketch033,Pad003,Sketch034,Pocket029,Pocket031,Sketch036,Sketch037,Pocket032,Mirrored004,Sketch038,Sketch039,Pocket033,Pocket034]
  Origin = -> Origin005
  Tip = -> Pocket034
COMPONENT P6 — same part as P5; its construction recipe is shown at P5.
COMPONENT P7 — recipe-attached ("Muntin single right001", modeled in this document).
Construction recipe (the document's own serialized feature program — sketch geometry with constraints, then the solid features built on it; lengths are millimeters unless a unit is written):

FEATURE [PartDesign::FeatureBase] BaseFeature003
  BaseFeature = -> Part__Mirroring002
  Suppressed = false
FEATURE [PartDesign::Body] Body007  label="Muntin single right"
  AllowCompound = false
  BaseFeature = -> Part__Mirroring002
  Group = -> [BaseFeature003]
  Origin = -> Origin007
  Tip = -> BaseFeature003
COMPONENT P8 — same part as P7; its construction recipe is shown at P7.
COMPONENT P9 — recipe-attached ("Rail bottom left001", modeled in this document).
Construction recipe (the document's own serialized feature program — sketch geometry with constraints, then the solid features built on it; lengths are millimeters unless a unit is written):

FEATURE [PartDesign::Plane] DatumPlane035  label="DatumPlane top007"
  AttachmentOffset = pos=(0,0,82.5) rot=(0,0,1;0rad)
  AttachmentSupport = -> [X_Axis010]
  Length = 610
  MapMode = 2
  Placement = pos=(0,0,82.5) rot=(0,0,1;0rad)
  ResizeMode = 1
  Width = 65
  expr: .AttachmentOffset.Base.z = <<Parameters>>.RailBottomWidth / 2
  expr: Length = <<Parameters>>.RailLength
  expr: Width = <<Parameters>>.WindowThickness
FEATURE [PartDesign::Plane] DatumPlane036  label="DatumPlane right006"
  AttachmentOffset = pos=(0,0,305) rot=(0,0,1;0rad)
  AttachmentSupport = -> [X_Axis010]
  Length = 65
  MapMode = 4
  Placement = pos=(305,0,0) rot=(0.57735,0.57735,0.57735;2.0944rad)
  ResizeMode = 1
  Width = 165
  expr: .AttachmentOffset.Base.z = <<Parameters>>.RailLength / 2
  expr: Length = <<Parameters>>.WindowThickness
  expr: Width = <<Parameters>>.RailBottomWidth
FEATURE [PartDesign::Plane] DatumPlane037  label="DatumPlane front006"
  AttachmentOffset = pos=(0,0,32.5) rot=(0,0,1;0rad)
  AttachmentSupport = -> [X_Axis010]
  Length = 610
  MapMode = 3
  Placement = pos=(0,-32.5,7.2e-15) rot=(1,0,0;1.5708rad)
  ResizeMode = 1
  Width = 165
  expr: .AttachmentOffset.Base.z = <<Parameters>>.WindowThickness / 2
  expr: Length = <<Parameters>>.RailLength
  expr: Width = <<Parameters>>.RailBottomWidth
FEATURE [PartDesign::Plane] DatumPlane038  label="DatumPlane left006"
  AttachmentOffset = pos=(0,0,305) rot=(0,0,1;0rad)
  AttachmentSupport = -> [X_Axis010]
  Length = 65
  MapMode = 4
  Placement = pos=(-305,0,0) rot=(0.57735,-0.57735,-0.57735;2.0944rad)
  ResizeMode = 1
  Width = 165
  expr: .AttachmentOffset.Base.z = <<Parameters>>.RailLength / 2
  expr: Length = <<Parameters>>.WindowThickness
  expr: Width = <<Parameters>>.RailBottomWidth
FEATURE [PartDesign::Plane] DatumPlane039  label="DatumPlane bottom003"
  AttachmentOffset = pos=(0,0,82.5) rot=(0,0,1;0rad)
  AttachmentSupport = -> [X_Axis010]
  Length = 610
  MapMode = 2
  Placement = pos=(0,0,-82.5) rot=(0,1,0;3.14159rad)
  ResizeMode = 1
  Width = 65
  expr: .AttachmentOffset.Base.z = <<Parameters>>.RailBottomWidth / 2
  expr: Length = <<Parameters>>.RailLength
  expr: Width = <<Parameters>>.WindowThickness
FEATURE [PartDesign::Plane] DatumPlane040  label="DatumPlane front007"
  AttachmentOffset = pos=(0,0,32.5) rot=(0,0,1;0rad)
  AttachmentSupport = -> [X_Axis010]
  Length = 610
  MapMode = 3
  Placement = pos=(0,32.5,-7.2e-15) rot=(0,0.707107,0.707107;3.14159rad)
  ResizeMode = 1
  Width = 165
  expr: .AttachmentOffset.Base.z = <<Parameters>>.WindowThickness / 2
  expr: Length = <<Parameters>>.RailLength
  expr: Width = <<Parameters>>.RailBottomWidth
FEATURE [Sketcher::SketchObject] Sketch053
  ArcFitTolerance = 0
  AttachmentSupport = -> [DatumPlane037]
  FullyConstrained = true
  MakeInternals = false
  MapMode = 5
  Placement = pos=(0,-32.5,7.2e-15) rot=(1,0,0;1.5708rad)
  expr: Constraints[10] = <<Parameters>>.RailLength
  expr: Constraints[11] = <<Parameters>>.RailBottomWidth
  sketch-geometry (5):
    g0: LineSegment StartX=-305 StartY=82.5 StartZ=0 EndX=-305 EndY=-82.5 EndZ=0
    g1: LineSegment StartX=-305 StartY=-82.5 StartZ=0 EndX=305 EndY=-82.5 EndZ=0
    g2: LineSegment StartX=305 StartY=-82.5 StartZ=0 EndX=305 EndY=82.5 EndZ=0
    g3: LineSegment StartX=305 StartY=82.5 StartZ=0 EndX=-305 EndY=82.5 EndZ=0
    g4: GeomPoint [constr] X=0 Y=0 Z=0
  constraints (12):
    c: Coincident(g0,g1)
    c: Coincident(g1,g2)
    c: Coincident(g2,g3)
    c: Coincident(g3,g0)
    c: Vertical(g0)
    c: Vertical(g2)
    c: Horizontal(g1)
    c: Horizontal(g3)
    c: Symmetric(g2,g0,g4)
    c: Coincident(g4,g-1)
    c: DistanceX(g3,g3) = 610
    c: DistanceY(g2,g2) = 165
FEATURE [PartDesign::Pad] Pad005  label="Stock005"
  Direction = (0,-1,2e-16)
  Length = 65
  Length2 = 10
  Placement = pos=(0,-32.5,7.2e-15) rot=(1,0,0;1.5708rad)
  Profile = -> Sketch053
  ReferenceAxis = -> Sketch053 [N_Axis]
  Refine = true
  Reversed = true
  Suppressed = false
  Type = 0
  expr: Length = <<Parameters>>.WindowThickness
FEATURE [Sketcher::SketchObject] Sketch054
  ArcFitTolerance = 0
  AttachmentSupport = -> [DatumPlane035]
  ExternalGeometry = -> [DatumPlane036,DatumPlane037]
  FullyConstrained = true
  MakeInternals = false
  MapMode = 5
  Placement = pos=(0,0,82.5) rot=(0,0,1;0rad)
  expr: Constraints[15] = <<Parameters>>.StileInnerWidth
  expr: Constraints[16] = <<Parameters>>.StileInnerWidth - <<Parameters>>.GlassRebateWidth
  expr: Constraints[17] = <<Parameters>>.GlassRebateDepth
  expr: Constraints[18] = <<Parameters>>.RailTenonThickness
  expr: Constraints[19] = <<Parameters>>.WindowThickness
  sketch-geometry (8):
    g0: LineSegment StartX=305 StartY=32.5 StartZ=0 EndX=245 EndY=32.5 EndZ=0
    g1: LineSegment StartX=245 StartY=32.5 StartZ=0 EndX=245 EndY=0.5 EndZ=0
    g2: LineSegment StartX=245 StartY=0.5 StartZ=0 EndX=305 EndY=0.5 EndZ=0
    g3: LineSegment StartX=305 StartY=0.5 StartZ=0 EndX=305 EndY=32.5 EndZ=0
    g4: LineSegment StartX=305 StartY=-32.5 StartZ=0 EndX=305 EndY=-14.5 EndZ=0
    g5: LineSegment StartX=305 StartY=-14.5 StartZ=0 EndX=235 EndY=-14.5 EndZ=0
    g6: LineSegment StartX=235 StartY=-14.5 StartZ=0 EndX=235 EndY=-32.5 EndZ=0
    g7: LineSegment StartX=235 StartY=-32.5 StartZ=0 EndX=305 EndY=-32.5 EndZ=0
  constraints (22):
    c: Coincident(g0,g1)
    c: Coincident(g1,g2)
    c: Coincident(g2,g3)
    c: Coincident(g3,g0)
    c: Horizontal(g0)
    c: Horizontal(g2)
    c: Vertical(g1)
    c: Coincident(g4,g5)
    c: Coincident(g5,g6)
    c: Coincident(g6,g7)
    c: Coincident(g7,g4)
    c: Vertical(g4)
    c: Vertical(g6)
    c: Horizontal(g5)
    c: Vertical(g4,g2)
    c: DistanceX(g7,g7) = 70
    c: DistanceX(g0,g0) = 60
    c: DistanceY(g3,g3) = 32
    c: Distance(g2,g4) = 15
    c: DistanceY(g4,g0) = 65
    c: Tangent(g3,g-3)
    c: Tangent(g7,g-4)
FEATURE [PartDesign::Pocket] Pocket047  label="Tenon inner002"
  BaseFeature = -> Pad005
  Direction = (0,0,-1)
  Length = 5
  Length2 = 5
  Placement = pos=(0,-32.5,7.2e-15) rot=(1,0,0;1.5708rad)
  Profile = -> Sketch054
  ReferenceAxis = -> Sketch054 [N_Axis]
  Refine = true
  Suppressed = false
  Type = 1
FEATURE [Sketcher::SketchObject] Sketch055
  ArcFitTolerance = 0
  AttachmentSupport = -> [DatumPlane035]
  ExternalGeometry = -> [DatumPlane037,DatumPlane038]
  FullyConstrained = true
  MakeInternals = false
  MapMode = 5
  Placement = pos=(0,0,82.5) rot=(0,0,1;0rad)
  expr: Constraints[15] = <<Parameters>>.WindowThickness
  expr: Constraints[16] = <<Parameters>>.GlassRebateDepth
  expr: Constraints[17] = <<Parameters>>.RailTenonThickness
  expr: Constraints[18] = <<Parameters>>.StileOuterWidth
  expr: Constraints[19] = <<Parameters>>.StileOuterWidth - <<Parameters>>.GlassRebateWidth
  sketch-geometry (8):
    g0: LineSegment StartX=-305 StartY=32.5 StartZ=0 EndX=-305 EndY=0.5 EndZ=0
    g1: LineSegment StartX=-305 StartY=0.5 StartZ=0 EndX=-225 EndY=0.5 EndZ=0
    g2: LineSegment StartX=-225 StartY=0.5 StartZ=0 EndX=-225 EndY=32.5 EndZ=0
    g3: LineSegment StartX=-225 StartY=32.5 StartZ=0 EndX=-305 EndY=32.5 EndZ=0
    g4: LineSegment StartX=-305 StartY=-14.5 StartZ=0 EndX=-305 EndY=-32.5 EndZ=0
    g5: LineSegment StartX=-305 StartY=-32.5 StartZ=0 EndX=-215 EndY=-32.5 EndZ=0
    g6: LineSegment StartX=-215 StartY=-32.5 StartZ=0 EndX=-215 EndY=-14.5 EndZ=0
    g7: LineSegment StartX=-215 StartY=-14.5 StartZ=0 EndX=-305 EndY=-14.5 EndZ=0
  constraints (22):
    c: Coincident(g0,g1)
    c: Coincident(g1,g2)
    c: Coincident(g2,g3)
    c: Coincident(g3,g0)
    c: Vertical(g2)
    c: Horizontal(g1)
    c: Horizontal(g3)
    c: Coincident(g4,g5)
    c: Coincident(g5,g6)
    c: Coincident(g6,g7)
    c: Coincident(g7,g4)
    c: Vertical(g4)
    c: Vertical(g6)
    c: Horizontal(g7)
    c: Vertical(g4,g0)
    c: DistanceY(g4,g0) = 65
    c: DistanceY(g2,g2) = 32
    c: DistanceY(g4,g0) = 15
    c: DistanceX(g5,g5) = 90
    c: DistanceX(g3,g3) = 80
    c: Tangent(g0,g-4)
    c: Tangent(g5,g-3)
FEATURE [PartDesign::Pocket] Pocket048  label="Tenon outer002"
  BaseFeature = -> Pocket047
  Direction = (0,0,-1)
  Length = 5
  Length2 = 5
  Placement = pos=(0,-32.5,7.2e-15) rot=(1,0,0;1.5708rad)
  Profile = -> Sketch055
  ReferenceAxis = -> Sketch055 [N_Axis]
  Refine = true
  Suppressed = false
  Type = 1
FEATURE [Sketcher::SketchObject] Sketch056
  ArcFitTolerance = 0
  AttachmentSupport = -> [DatumPlane037]
  ExternalGeometry = -> [DatumPlane036,DatumPlane039]
  FullyConstrained = true
  MakeInternals = false
  MapMode = 5
  Placement = pos=(0,-32.5,7.2e-15) rot=(1,0,0;1.5708rad)
  expr: Constraints[5] = <<Parameters>>.RailBottomWidth - <<Parameters>>.RailBottomTenonWidth
  expr: Constraints[6] = <<Parameters>>.StileInnerWidth - <<Parameters>>.StileInnerHaunchDepth
  sketch-geometry (4):
    g0: LineSegment StartX=305 StartY=-17.5 StartZ=0 EndX=255 EndY=-17.5 EndZ=0
    g1: LineSegment StartX=255 StartY=-17.5 StartZ=0 EndX=255 EndY=-82.5 EndZ=0
    g2: LineSegment StartX=255 StartY=-82.5 StartZ=0 EndX=305 EndY=-82.5 EndZ=0
    g3: LineSegment StartX=305 StartY=-82.5 StartZ=0 EndX=305 EndY=-17.5 EndZ=0
  constraints (10):
    c: Coincident(g0,g1)
    c: Coincident(g1,g2)
    c: Coincident(g2,g3)
    c: Coincident(g3,g0)
    c: Vertical(g1)
    c: DistanceY(g3,g3) = 65
    c: DistanceX(g0,g0) = 50
    c: Tangent(g3,g-3)
    c: Horizontal(g0,g0)
    c: Tangent(g2,g-4)
FEATURE [PartDesign::Pocket] Pocket049  label="Haunch inner001"
  BaseFeature = -> Pocket048
  Direction = (0,1,-2e-16)
  Length = 5
  Length2 = 5
  Placement = pos=(0,-32.5,7.2e-15) rot=(1,0,0;1.5708rad)
  Profile = -> Sketch056
  ReferenceAxis = -> Sketch056 [N_Axis]
  Refine = true
  Suppressed = false
  Type = 1
FEATURE [Sketcher::SketchObject] Sketch057
  ArcFitTolerance = 0
  AttachmentSupport = -> [DatumPlane037]
  ExternalGeometry = -> [DatumPlane038,DatumPlane039]
  FullyConstrained = true
  MakeInternals = false
  MapMode = 5
  Placement = pos=(0,-32.5,7.2e-15) rot=(1,0,0;1.5708rad)
  expr: Constraints[5] = <<Parameters>>.StileOuterWidth - <<Parameters>>.StileOuterHaunchDepth
  expr: Constraints[6] = <<Parameters>>.RailBottomWidth - <<Parameters>>.RailBottomTenonWidth
  sketch-geometry (4):
    g0: LineSegment StartX=-305 StartY=-17.5 StartZ=0 EndX=-305 EndY=-82.5 EndZ=0
    g1: LineSegment StartX=-305 StartY=-82.5 StartZ=0 EndX=-240 EndY=-82.5 EndZ=0
    g2: LineSegment StartX=-240 StartY=-82.5 StartZ=0 EndX=-240 EndY=-17.5 EndZ=0
    g3: LineSegment StartX=-240 StartY=-17.5 StartZ=0 EndX=-305 EndY=-17.5 EndZ=0
  constraints (10):
    c: Coincident(g0,g1)
    c: Coincident(g1,g2)
    c: Coincident(g2,g3)
    c: Coincident(g3,g0)
    c: Vertical(g2)
    c: DistanceX(g3,g3) = 65
    c: DistanceY(g0,g0) = 65
    c: Tangent(g-3,g0)
    c: Horizontal(g0,g2)
    c: Tangent(g1,g-4)
FEATURE [PartDesign::Pocket] Pocket050  label="Haunch outer001"
  BaseFeature = -> Pocket049
  Direction = (0,1,-2e-16)
  Length = 5
  Length2 = 5
  Placement = pos=(0,-32.5,7.2e-15) rot=(1,0,0;1.5708rad)
  Profile = -> Sketch057
  ReferenceAxis = -> Sketch057 [N_Axis]
  Refine = true
  Suppressed = false
  Type = 1
FEATURE [Sketcher::SketchObject] Sketch059
  ArcFitTolerance = 0
  AttachmentSupport = -> [DatumPlane035]
  ExternalGeometry = -> [DatumPlane040]
  FullyConstrained = true
  MakeInternals = false
  MapMode = 5
  Placement = pos=(0,0,82.5) rot=(0,0,1;0rad)
  expr: Constraints[10] = <<Parameters>>.GlassRebateDepth
  expr: Constraints[7] = <<Parameters>>.RailLength
  expr: Constraints[8] = <<Parameters>>.GlassRebateDepth
  sketch-geometry (4):
    g0: LineSegment StartX=-305 StartY=32.5 StartZ=0 EndX=-305 EndY=0.5 EndZ=0
    g1: LineSegment StartX=-305 StartY=0.5 StartZ=0 EndX=305 EndY=0.5 EndZ=0
    g2: LineSegment StartX=305 StartY=0.5 StartZ=0 EndX=305 EndY=32.5 EndZ=0
    g3: LineSegment StartX=305 StartY=32.5 StartZ=0 EndX=-305 EndY=32.5 EndZ=0
  constraints (11):
    c: Coincident(g0,g1)
    c: Coincident(g1,g2)
    c: Coincident(g2,g3)
    c: Coincident(g3,g0)
    c: Vertical(g0)
    c: Vertical(g2)
    c: Horizontal(g1)
    c: DistanceX(g3,g3) = 610
    c: DistanceY(g0,g0) = 32
    c: Symmetric(g0,g2,g-2)
    c: Distance(g0,g-3) = 32
FEATURE [PartDesign::Pocket] Pocket052  label="Glass rebate003"
  BaseFeature = -> Pocket050
  Direction = (0,0,-1)
  Length = 10
  Length2 = 5
  Placement = pos=(0,-32.5,7.2e-15) rot=(1,0,0;1.5708rad)
  Profile = -> Sketch059
  ReferenceAxis = -> Sketch059 [N_Axis]
  Refine = true
  Suppressed = false
  Type = 0
  expr: Length = <<Parameters>>.GlassRebateWidth
FEATURE [Sketcher::SketchObject] Sketch060
  ArcFitTolerance = 0
  AttachmentSupport = -> [DatumPlane036]
  ExternalGeometry = -> [DatumPlane040,DatumPlane039]
  FullyConstrained = true
  MakeInternals = false
  MapMode = 5
  Placement = pos=(305,0,0) rot=(0.57735,0.57735,0.57735;2.0944rad)
  expr: Constraints[5] = <<Parameters>>.WindowFrameRebateWidth
  expr: Constraints[6] = <<Parameters>>.WindowFrameRebateDepth
  sketch-geometry (4):
    g0: LineSegment StartX=12.5 StartY=-57.5 StartZ=0 EndX=12.5 EndY=-82.5 EndZ=0
    g1: LineSegment StartX=12.5 StartY=-82.5 StartZ=0 EndX=32.5 EndY=-82.5 EndZ=0
    g2: LineSegment StartX=32.5 StartY=-82.5 StartZ=0 EndX=32.5 EndY=-57.5 EndZ=0
    g3: LineSegment StartX=32.5 StartY=-57.5 StartZ=0 EndX=12.5 EndY=-57.5 EndZ=0
  constraints (10):
    c: Coincident(g0,g1)
    c: Coincident(g1,g2)
    c: Coincident(g2,g3)
    c: Coincident(g3,g0)
    c: Vertical(g0)
    c: DistanceX(g3,g3) = 20
    c: DistanceY(g2,g2) = 25
    c: Tangent(g2,g-3)
    c: Tangent(g1,g-4)
    c: Horizontal(g0,g2)
FEATURE [PartDesign::Pocket] Pocket053  label="Frame rebate opening top006"
  BaseFeature = -> Pocket052
  Direction = (-1,0,0)
  Length = 5
  Length2 = 5
  Placement = pos=(0,-32.5,7.2e-15) rot=(1,0,0;1.5708rad)
  Profile = -> Sketch060
  ReferenceAxis = -> Sketch060 [N_Axis]
  Refine = true
  Suppressed = false
  Type = 1
FEATURE [Sketcher::SketchObject] Sketch061
  ArcFitTolerance = 0
  AttachmentSupport = -> [DatumPlane036]
  ExternalGeometry = -> [DatumPlane040,DatumPlane039]
  FullyConstrained = true
  MakeInternals = false
  MapMode = 5
  Placement = pos=(305,0,0) rot=(0.57735,0.57735,0.57735;2.0944rad)
  expr: Constraints[5] = <<Parameters>>.WindowInnerLipWidth
  expr: Constraints[6] = <<Parameters>>.FrameThickness
  sketch-geometry (4):
    g0: LineSegment StartX=32.5 StartY=-67.5 StartZ=0 EndX=-17.5 EndY=-67.5 EndZ=0
    g1: LineSegment StartX=-17.5 StartY=-67.5 StartZ=0 EndX=-17.5 EndY=-82.5 EndZ=0
    g2: LineSegment StartX=-17.5 StartY=-82.5 StartZ=0 EndX=32.5 EndY=-82.5 EndZ=0
    g3: LineSegment StartX=32.5 StartY=-82.5 StartZ=0 EndX=32.5 EndY=-67.5 EndZ=0
  constraints (10):
    c: Coincident(g0,g1)
    c: Coincident(g1,g2)
    c: Coincident(g2,g3)
    c: Coincident(g3,g0)
    c: Vertical(g1)
    c: DistanceY(g3,g3) = 15
    c: DistanceX(g0,g0) = 50
    c: Tangent(g3,g-3)
    c: Horizontal(g0,g0)
    c: Tangent(g2,g-4)
FEATURE [PartDesign::Pocket] Pocket054  label="Frame rebate lip top005"
  BaseFeature = -> Pocket053
  Direction = (-1,0,0)
  Length = 5
  Length2 = 5
  Placement = pos=(0,-32.5,7.2e-15) rot=(1,0,0;1.5708rad)
  Profile = -> Sketch061
  ReferenceAxis = -> Sketch061 [N_Axis]
  Refine = true
  Suppressed = false
  Type = 1
FEATURE [Sketcher::SketchObject] Sketch062
  ArcFitTolerance = 0
  AttachmentSupport = -> [DatumPlane035]
  ExternalGeometry = -> [DatumPlane040,DatumPlane038]
  FullyConstrained = true
  MakeInternals = false
  MapMode = 5
  Placement = pos=(0,0,82.5) rot=(0,0,1;0rad)
  expr: Constraints[6] = <<Parameters>>.WindowInnerLipWidth
  expr: Constraints[7] = <<Parameters>>.WindowThickness
  sketch-geometry (4):
    g0: LineSegment StartX=-305 StartY=32.5 StartZ=0 EndX=-305 EndY=-32.5 EndZ=0
    g1: LineSegment StartX=-305 StartY=-32.5 StartZ=0 EndX=-290 EndY=-32.5 EndZ=0
    g2: LineSegment StartX=-290 StartY=-32.5 StartZ=0 EndX=-290 EndY=32.5 EndZ=0
    g3: LineSegment StartX=-290 StartY=32.5 StartZ=0 EndX=-305 EndY=32.5 EndZ=0
  constraints (10):
    c: Coincident(g0,g1)
    c: Coincident(g1,g2)
    c: Coincident(g2,g3)
    c: Coincident(g3,g0)
    c: Vertical(g2)
    c: Horizontal(g1)
    c: DistanceX(g3,g3) = 15
    c: DistanceY(g0,g0) = 65
    c: Tangent(g3,g-3)
    c: Tangent(g0,g-4)
FEATURE [PartDesign::Pocket] Pocket055  label="Frame rebate lip left002"
  BaseFeature = -> Pocket054
  Direction = (0,0,-1)
  Length = 5
  Length2 = 5
  Placement = pos=(0,-32.5,7.2e-15) rot=(1,0,0;1.5708rad)
  Profile = -> Sketch062
  ReferenceAxis = -> Sketch062 [N_Axis]
  Refine = true
  Suppressed = false
  Type = 1
FEATURE [Sketcher::SketchObject] Sketch063
  ArcFitTolerance = 0
  AttachmentSupport = -> [DatumPlane035]
  ExternalGeometry = -> [DatumPlane036,DatumPlane037]
  FullyConstrained = true
  MakeInternals = false
  MapMode = 5
  Placement = pos=(0,0,82.5) rot=(0,0,1;0rad)
  expr: Constraints[6] = <<Parameters>>.IntersectionRebateDepth
  expr: Constraints[7] = <<Parameters>>.IntersectionRebateWidth
  sketch-geometry (4):
    g0: LineSegment StartX=305 StartY=-5.68e-14 StartZ=0 EndX=295 EndY=-5.68e-14 EndZ=0
    g1: LineSegment StartX=295 StartY=-5.68e-14 StartZ=0 EndX=295 EndY=-32.5 EndZ=0
    g2: LineSegment StartX=295 StartY=-32.5 StartZ=0 EndX=305 EndY=-32.5 EndZ=0
    g3: LineSegment StartX=305 StartY=-32.5 StartZ=0 EndX=305 EndY=-5.68e-14 EndZ=0
  constraints (10):
    c: Coincident(g0,g1)
    c: Coincident(g1,g2)
    c: Coincident(g2,g3)
    c: Coincident(g3,g0)
    c: Horizontal(g0)
    c: Vertical(g1)
    c: DistanceX(g2,g2) = 10
    c: DistanceY(g3,g3) = 32.5
    c: Tangent(g2,g-4)
    c: Tangent(g3,g-3)
FEATURE [PartDesign::Pocket] Pocket056  label="Frame rebate intersection right001"
  BaseFeature = -> Pocket055
  Direction = (0,0,-1)
  Length = 5
  Length2 = 5
  Placement = pos=(0,-32.5,7.2e-15) rot=(1,0,0;1.5708rad)
  Profile = -> Sketch063
  ReferenceAxis = -> Sketch063 [N_Axis]
  Refine = true
  Suppressed = false
  Type = 1
FEATURE [PartDesign::Body] Body010  label="Rail bottom left"
  AllowCompound = false
  Group = -> [DatumPlane035,DatumPlane036,DatumPlane037,DatumPlane038,DatumPlane039,DatumPlane040,Sketch053,Pad005,Sketch054,Pocket047,Sketch055,Pocket048,Sketch056,Pocket049,Sketch057,Pocket050,Sketch059,Pocket052,Sketch060,Pocket053,Sketch061,Pocket054,Sketch062,Sketch063,Pocket055,Pocket056]
  Origin = -> Origin010
  Tip = -> Pocket056
COMPONENT P10 — recipe-attached ("Rail bottom right001", modeled in this document).
Construction recipe (the document's own serialized feature program — sketch geometry with constraints, then the solid features built on it; lengths are millimeters unless a unit is written):

FEATURE [PartDesign::FeatureBase] BaseFeature006
  BaseFeature = -> Part__Mirroring005
  Suppressed = false
FEATURE [PartDesign::Body] Body012  label="Rail bottom right"
  AllowCompound = false
  BaseFeature = -> Part__Mirroring005
  Group = -> [BaseFeature006]
  Origin = -> Origin012
  Tip = -> BaseFeature006
COMPONENT P11 — recipe-attached ("Rail top left001", modeled in this document).
Construction recipe (the document's own serialized feature program — sketch geometry with constraints, then the solid features built on it; lengths are millimeters unless a unit is written):

FEATURE [PartDesign::Plane] DatumPlane028  label="DatumPlane top006"
  AttachmentOffset = pos=(0,0,57.5) rot=(0,0,1;0rad)
  AttachmentSupport = -> [X_Axis009]
  Length = 610
  MapMode = 2
  Placement = pos=(0,0,57.5) rot=(0,0,1;0rad)
  ResizeMode = 1
  Width = 65
  expr: .AttachmentOffset.Base.z = <<Parameters>>.RailTopWidth / 2
  expr: Length = <<Parameters>>.RailLength
  expr: Width = <<Parameters>>.WindowThickness
FEATURE [PartDesign::Plane] DatumPlane029  label="DatumPlane right005"
  AttachmentOffset = pos=(0,0,305) rot=(0,0,1;0rad)
  AttachmentSupport = -> [X_Axis009]
  Length = 65
  MapMode = 4
  Placement = pos=(305,0,0) rot=(0.57735,0.57735,0.57735;2.0944rad)
  ResizeMode = 1
  Width = 115
  expr: .AttachmentOffset.Base.z = <<Parameters>>.RailLength / 2
  expr: Length = <<Parameters>>.WindowThickness
  expr: Width = <<Parameters>>.RailTopWidth
FEATURE [PartDesign::Plane] DatumPlane031  label="DatumPlane front004"
  AttachmentOffset = pos=(0,0,32.5) rot=(0,0,1;0rad)
  AttachmentSupport = -> [X_Axis009]
  Length = 610
  MapMode = 3
  Placement = pos=(0,-32.5,7.2e-15) rot=(1,0,0;1.5708rad)
  ResizeMode = 1
  Width = 115
  expr: .AttachmentOffset.Base.z = <<Parameters>>.WindowThickness / 2
  expr: Length = <<Parameters>>.RailLength
  expr: Width = <<Parameters>>.RailTopWidth
FEATURE [Sketcher::SketchObject] Sketch042
  ArcFitTolerance = 0
  AttachmentSupport = -> [DatumPlane031]
  FullyConstrained = true
  MakeInternals = false
  MapMode = 5
  Placement = pos=(0,-32.5,7.2e-15) rot=(1,0,0;1.5708rad)
  expr: Constraints[10] = <<Parameters>>.RailLength
  expr: Constraints[11] = <<Parameters>>.RailTopWidth
  sketch-geometry (5):
    g0: LineSegment StartX=-305 StartY=57.5 StartZ=0 EndX=-305 EndY=-57.5 EndZ=0
    g1: LineSegment StartX=-305 StartY=-57.5 StartZ=0 EndX=305 EndY=-57.5 EndZ=0
    g2: LineSegment StartX=305 StartY=-57.5 StartZ=0 EndX=305 EndY=57.5 EndZ=0
    g3: LineSegment StartX=305 StartY=57.5 StartZ=0 EndX=-305 EndY=57.5 EndZ=0
    g4: GeomPoint [constr] X=0 Y=0 Z=0
  constraints (12):
    c: Coincident(g0,g1)
    c: Coincident(g1,g2)
    c: Coincident(g2,g3)
    c: Coincident(g3,g0)
    c: Vertical(g0)
    c: Vertical(g2)
    c: Horizontal(g1)
    c: Horizontal(g3)
    c: Symmetric(g2,g0,g4)
    c: Coincident(g4,g-1)
    c: DistanceX(g3,g3) = 610
    c: DistanceY(g2,g2) = 115
FEATURE [PartDesign::Pad] Pad004  label="Stock004"
  Direction = (0,-1,2e-16)
  Length = 65
  Length2 = 10
  Placement = pos=(0,-32.5,7.2e-15) rot=(1,0,0;1.5708rad)
  Profile = -> Sketch042
  ReferenceAxis = -> Sketch042 [N_Axis]
  Refine = true
  Reversed = true
  Suppressed = false
  Type = 0
  expr: Length = <<Parameters>>.WindowThickness
FEATURE [Sketcher::SketchObject] Sketch043
  ArcFitTolerance = 0
  AttachmentSupport = -> [DatumPlane028]
  ExternalGeometry = -> [DatumPlane029,DatumPlane031]
  FullyConstrained = true
  MakeInternals = false
  MapMode = 5
  Placement = pos=(0,0,57.5) rot=(0,0,1;0rad)
  expr: Constraints[15] = <<Parameters>>.StileInnerWidth
  expr: Constraints[16] = <<Parameters>>.StileInnerWidth - <<Parameters>>.GlassRebateWidth
  expr: Constraints[17] = <<Parameters>>.GlassRebateDepth
  expr: Constraints[18] = <<Parameters>>.RailTenonThickness
  expr: Constraints[19] = <<Parameters>>.WindowThickness
  sketch-geometry (8):
    g0: LineSegment StartX=305 StartY=32.5 StartZ=0 EndX=245 EndY=32.5 EndZ=0
    g1: LineSegment StartX=245 StartY=32.5 StartZ=0 EndX=245 EndY=0.5 EndZ=0
    g2: LineSegment StartX=245 StartY=0.5 StartZ=0 EndX=305 EndY=0.5 EndZ=0
    g3: LineSegment StartX=305 StartY=0.5 StartZ=0 EndX=305 EndY=32.5 EndZ=0
    g4: LineSegment StartX=305 StartY=-32.5 StartZ=0 EndX=305 EndY=-14.5 EndZ=0
    g5: LineSegment StartX=305 StartY=-14.5 StartZ=0 EndX=235 EndY=-14.5 EndZ=0
    g6: LineSegment StartX=235 StartY=-14.5 StartZ=0 EndX=235 EndY=-32.5 EndZ=0
    g7: LineSegment StartX=235 StartY=-32.5 StartZ=0 EndX=305 EndY=-32.5 EndZ=0
  constraints (22):
    c: Coincident(g0,g1)
    c: Coincident(g1,g2)
    c: Coincident(g2,g3)
    c: Coincident(g3,g0)
    c: Horizontal(g0)
    c: Horizontal(g2)
    c: Vertical(g1)
    c: Coincident(g4,g5)
    c: Coincident(g5,g6)
    c: Coincident(g6,g7)
    c: Coincident(g7,g4)
    c: Vertical(g4)
    c: Vertical(g6)
    c: Horizontal(g5)
    c: Vertical(g4,g2)
    c: DistanceX(g7,g7) = 70
    c: DistanceX(g0,g0) = 60
    c: DistanceY(g3,g3) = 32
    c: Distance(g2,g4) = 15
    c: DistanceY(g4,g0) = 65
    c: Tangent(g3,g-3)
    c: Tangent(g7,g-4)
FEATURE [PartDesign::Plane] DatumPlane032  label="DatumPlane left005"
  AttachmentOffset = pos=(0,0,305) rot=(0,0,1;0rad)
  AttachmentSupport = -> [X_Axis009]
  Length = 65
  MapMode = 4
  Placement = pos=(-305,0,0) rot=(0.57735,-0.57735,-0.57735;2.0944rad)
  ResizeMode = 1
  Width = 115
  expr: .AttachmentOffset.Base.z = <<Parameters>>.RailLength / 2
  expr: Length = <<Parameters>>.WindowThickness
  expr: Width = <<Parameters>>.RailTopWidth
FEATURE [PartDesign::Pocket] Pocket037  label="Tenon inner001"
  BaseFeature = -> Pad004
  Direction = (0,0,-1)
  Length = 5
  Length2 = 5
  Placement = pos=(0,-32.5,7.2e-15) rot=(1,0,0;1.5708rad)
  Profile = -> Sketch043
  ReferenceAxis = -> Sketch043 [N_Axis]
  Refine = true
  Suppressed = false
  Type = 1
FEATURE [Sketcher::SketchObject] Sketch044
  ArcFitTolerance = 0
  AttachmentSupport = -> [DatumPlane028]
  ExternalGeometry = -> [DatumPlane031,DatumPlane032]
  FullyConstrained = true
  MakeInternals = false
  MapMode = 5
  Placement = pos=(0,0,57.5) rot=(0,0,1;0rad)
  expr: Constraints[15] = <<Parameters>>.WindowThickness
  expr: Constraints[16] = <<Parameters>>.GlassRebateDepth
  expr: Constraints[17] = <<Parameters>>.RailTenonThickness
  expr: Constraints[18] = <<Parameters>>.StileOuterWidth
  expr: Constraints[19] = <<Parameters>>.StileOuterWidth - <<Parameters>>.GlassRebateWidth
  sketch-geometry (8):
    g0: LineSegment StartX=-305 StartY=32.5 StartZ=0 EndX=-305 EndY=0.5 EndZ=0
    g1: LineSegment StartX=-305 StartY=0.5 StartZ=0 EndX=-225 EndY=0.5 EndZ=0
    g2: LineSegment StartX=-225 StartY=0.5 StartZ=0 EndX=-225 EndY=32.5 EndZ=0
    g3: LineSegment StartX=-225 StartY=32.5 StartZ=0 EndX=-305 EndY=32.5 EndZ=0
    g4: LineSegment StartX=-305 StartY=-14.5 StartZ=0 EndX=-305 EndY=-32.5 EndZ=0
    g5: LineSegment StartX=-305 StartY=-32.5 StartZ=0 EndX=-215 EndY=-32.5 EndZ=0
    g6: LineSegment StartX=-215 StartY=-32.5 StartZ=0 EndX=-215 EndY=-14.5 EndZ=0
    g7: LineSegment StartX=-215 StartY=-14.5 StartZ=0 EndX=-305 EndY=-14.5 EndZ=0
  constraints (22):
    c: Coincident(g0,g1)
    c: Coincident(g1,g2)
    c: Coincident(g2,g3)
    c: Coincident(g3,g0)
    c: Vertical(g2)
    c: Horizontal(g1)
    c: Horizontal(g3)
    c: Coincident(g4,g5)
    c: Coincident(g5,g6)
    c: Coincident(g6,g7)
    c: Coincident(g7,g4)
    c: Vertical(g4)
    c: Vertical(g6)
    c: Horizontal(g7)
    c: Vertical(g4,g0)
    c: DistanceY(g4,g0) = 65
    c: DistanceY(g2,g2) = 32
    c: DistanceY(g4,g0) = 15
    c: DistanceX(g5,g5) = 90
    c: DistanceX(g3,g3) = 80
    c: Tangent(g0,g-4)
    c: Tangent(g5,g-3)
FEATURE [PartDesign::Pocket] Pocket038  label="Tenon outer001"
  BaseFeature = -> Pocket037
  Direction = (0,0,-1)
  Length = 5
  Length2 = 5
  Placement = pos=(0,-32.5,7.2e-15) rot=(1,0,0;1.5708rad)
  Profile = -> Sketch044
  ReferenceAxis = -> Sketch044 [N_Axis]
  Refine = true
  Suppressed = false
  Type = 1
FEATURE [Sketcher::SketchObject] Sketch045
  ArcFitTolerance = 0
  AttachmentSupport = -> [DatumPlane031]
  ExternalGeometry = -> [DatumPlane028,DatumPlane029]
  FullyConstrained = true
  MakeInternals = false
  MapMode = 5
  Placement = pos=(0,-32.5,7.2e-15) rot=(1,0,0;1.5708rad)
  expr: Constraints[6] = <<Parameters>>.RailTopWidth - <<Parameters>>.RailTopTenonWidth
  expr: Constraints[7] = <<Parameters>>.StileInnerWidth - <<Parameters>>.StileInnerHaunchDepth
  sketch-geometry (4):
    g0: LineSegment StartX=305 StartY=57.5 StartZ=0 EndX=255 EndY=57.5 EndZ=0
    g1: LineSegment StartX=255 StartY=57.5 StartZ=0 EndX=255 EndY=12.5 EndZ=0
    g2: LineSegment StartX=255 StartY=12.5 StartZ=0 EndX=305 EndY=12.5 EndZ=0
    g3: LineSegment StartX=305 StartY=12.5 StartZ=0 EndX=305 EndY=57.5 EndZ=0
  constraints (10):
    c: Coincident(g0,g1)
    c: Coincident(g1,g2)
    c: Coincident(g2,g3)
    c: Coincident(g3,g0)
    c: Horizontal(g2)
    c: Vertical(g1)
    c: DistanceY(g3,g3) = 45
    c: DistanceX(g0,g0) = 50
    c: Tangent(g3,g-4)
    c: Tangent(g0,g-3)
FEATURE [PartDesign::Pocket] Pocket039  label="Haunch inner"
  BaseFeature = -> Pocket038
  Direction = (0,1,-2e-16)
  Length = 5
  Length2 = 5
  Placement = pos=(0,-32.5,7.2e-15) rot=(1,0,0;1.5708rad)
  Profile = -> Sketch045
  ReferenceAxis = -> Sketch045 [N_Axis]
  Refine = true
  Suppressed = false
  Type = 1
FEATURE [Sketcher::SketchObject] Sketch046
  ArcFitTolerance = 0
  AttachmentSupport = -> [DatumPlane031]
  ExternalGeometry = -> [DatumPlane028,DatumPlane032]
  FullyConstrained = true
  MakeInternals = false
  MapMode = 5
  Placement = pos=(0,-32.5,7.2e-15) rot=(1,0,0;1.5708rad)
  expr: Constraints[6] = <<Parameters>>.StileOuterWidth - <<Parameters>>.StileOuterHaunchDepth
  expr: Constraints[7] = <<Parameters>>.RailTopWidth - <<Parameters>>.RailTopTenonWidth
  sketch-geometry (4):
    g0: LineSegment StartX=-305 StartY=57.5 StartZ=0 EndX=-305 EndY=12.5 EndZ=0
    g1: LineSegment StartX=-305 StartY=12.5 StartZ=0 EndX=-240 EndY=12.5 EndZ=0
    g2: LineSegment StartX=-240 StartY=12.5 StartZ=0 EndX=-240 EndY=57.5 EndZ=0
    g3: LineSegment StartX=-240 StartY=57.5 StartZ=0 EndX=-305 EndY=57.5 EndZ=0
  constraints (10):
    c: Coincident(g0,g1)
    c: Coincident(g1,g2)
    c: Coincident(g2,g3)
    c: Coincident(g3,g0)
    c: Vertical(g2)
    c: Horizontal(g1)
    c: DistanceX(g3,g3) = 65
    c: DistanceY(g0,g0) = 45
    c: Tangent(g3,g-3)
    c: Tangent(g-4,g0)
FEATURE [PartDesign::Pocket] Pocket040  label="Haunch outer"
  BaseFeature = -> Pocket039
  Direction = (0,1,-2e-16)
  Length = 5
  Length2 = 5
  Placement = pos=(0,-32.5,7.2e-15) rot=(1,0,0;1.5708rad)
  Profile = -> Sketch046
  ReferenceAxis = -> Sketch046 [N_Axis]
  Refine = true
  Suppressed = false
  Type = 1
FEATURE [PartDesign::Plane] DatumPlane033  label="DatumPlane bottom002"
  AttachmentOffset = pos=(0,0,57.5) rot=(0,0,1;0rad)
  AttachmentSupport = -> [X_Axis009]
  Length = 610
  MapMode = 2
  Placement = pos=(0,0,-57.5) rot=(0,1,0;3.14159rad)
  ResizeMode = 1
  Width = 65
  expr: .AttachmentOffset.Base.z = <<Parameters>>.RailTopWidth / 2
  expr: Length = <<Parameters>>.RailLength
  expr: Width = <<Parameters>>.WindowThickness
FEATURE [PartDesign::Plane] DatumPlane034  label="DatumPlane front005"
  AttachmentOffset = pos=(0,0,32.5) rot=(0,0,1;0rad)
  AttachmentSupport = -> [X_Axis009]
  Length = 610
  MapMode = 3
  Placement = pos=(0,32.5,-7.2e-15) rot=(0,0.707107,0.707107;3.14159rad)
  ResizeMode = 1
  Width = 115
  expr: .AttachmentOffset.Base.z = <<Parameters>>.WindowThickness / 2
  expr: Length = <<Parameters>>.RailLength
  expr: Width = <<Parameters>>.RailTopWidth
FEATURE [Sketcher::SketchObject] Sketch047
  ArcFitTolerance = 0
  AttachmentSupport = -> [DatumPlane033]
  ExternalGeometry = -> [DatumPlane034,DatumPlane029]
  FullyConstrained = true
  MakeInternals = false
  MapMode = 5
  Placement = pos=(0,0,-57.5) rot=(0,1,0;3.14159rad)
  expr: Constraints[10] = <<Parameters>>.GlassRebateDepth
  expr: Constraints[11] = <<Parameters>>.GlassOpeningWidth / 2 - <<Parameters>>.MuntinWidth / 2 + <<Parameters>>.StileInnerWidth
  expr: Constraints[8] = <<Parameters>>.MuntinWidth
  expr: Constraints[9] = <<Parameters>>.MuntinTenonThickness
  sketch-geometry (4):
    g0: LineSegment StartX=-25 StartY=0.5 StartZ=0 EndX=-25 EndY=-9.5 EndZ=0
    g1: LineSegment StartX=-25 StartY=-9.5 StartZ=0 EndX=5 EndY=-9.5 EndZ=0
    g2: LineSegment StartX=5 StartY=-9.5 StartZ=0 EndX=5 EndY=0.5 EndZ=0
    g3: LineSegment StartX=5 StartY=0.5 StartZ=0 EndX=-25 EndY=0.5 EndZ=0
  constraints (12):
    c: Coincident(g0,g1)
    c: Coincident(g1,g2)
    c: Coincident(g2,g3)
    c: Coincident(g3,g0)
    c: Vertical(g0)
    c: Vertical(g2)
    c: Horizontal(g1)
    c: Horizontal(g3)
    c: DistanceX(g1,g1) = 30
    c: DistanceY(g2,g2) = 10
    c: Distance(g2,g-3) = 32
    c: Distance(g0,g-4) = 280
FEATURE [PartDesign::Pocket] Pocket041  label="Muntin bar mortise001"
  BaseFeature = -> Pocket040
  Direction = (0,0,1)
  Length = 15
  Length2 = 5
  Placement = pos=(0,-32.5,7.2e-15) rot=(1,0,0;1.5708rad)
  Profile = -> Sketch047
  ReferenceAxis = -> Sketch047 [N_Axis]
  Refine = true
  Suppressed = false
  Type = 0
  expr: Length = <<Parameters>>.MuntinBarTenonLength
FEATURE [Sketcher::SketchObject] Sketch048
  ArcFitTolerance = 0
  AttachmentSupport = -> [DatumPlane033]
  ExternalGeometry = -> [DatumPlane034]
  FullyConstrained = true
  MakeInternals = false
  MapMode = 5
  Placement = pos=(0,0,-57.5) rot=(0,1,0;3.14159rad)
  expr: Constraints[10] = <<Parameters>>.GlassRebateDepth
  expr: Constraints[7] = <<Parameters>>.RailLength
  expr: Constraints[8] = <<Parameters>>.GlassRebateDepth
  sketch-geometry (4):
    g0: LineSegment StartX=-305 StartY=32.5 StartZ=0 EndX=-305 EndY=0.5 EndZ=0
    g1: LineSegment StartX=-305 StartY=0.5 StartZ=0 EndX=305 EndY=0.5 EndZ=0
    g2: LineSegment StartX=305 StartY=0.5 StartZ=0 EndX=305 EndY=32.5 EndZ=0
    g3: LineSegment StartX=305 StartY=32.5 StartZ=0 EndX=-305 EndY=32.5 EndZ=0
  constraints (11):
    c: Coincident(g0,g1)
    c: Coincident(g1,g2)
    c: Coincident(g2,g3)
    c: Coincident(g3,g0)
    c: Vertical(g0)
    c: Vertical(g2)
    c: Horizontal(g1)
    c: DistanceX(g3,g3) = 610
    c: DistanceY(g0,g0) = 32
    c: Symmetric(g0,g2,g-2)
    c: Distance(g0,g-3) = 32
FEATURE [PartDesign::Pocket] Pocket042  label="Glass rebate002"
  BaseFeature = -> Pocket041
  Direction = (0,0,1)
  Length = 10
  Length2 = 5
  Placement = pos=(0,-32.5,7.2e-15) rot=(1,0,0;1.5708rad)
  Profile = -> Sketch048
  ReferenceAxis = -> Sketch048 [N_Axis]
  Refine = true
  Suppressed = false
  Type = 0
  expr: Length = <<Parameters>>.GlassRebateWidth
FEATURE [Sketcher::SketchObject] Sketch049
  ArcFitTolerance = 0
  AttachmentSupport = -> [DatumPlane029]
  ExternalGeometry = -> [DatumPlane028,DatumPlane034]
  FullyConstrained = true
  MakeInternals = false
  MapMode = 5
  Placement = pos=(305,0,0) rot=(0.57735,0.57735,0.57735;2.0944rad)
  expr: Constraints[6] = <<Parameters>>.WindowFrameRebateWidth
  expr: Constraints[7] = <<Parameters>>.WindowFrameRebateDepth
  sketch-geometry (4):
    g0: LineSegment StartX=12.5 StartY=57.5 StartZ=0 EndX=12.5 EndY=32.5 EndZ=0
    g1: LineSegment StartX=12.5 StartY=32.5 StartZ=0 EndX=32.5 EndY=32.5 EndZ=0
    g2: LineSegment StartX=32.5 StartY=32.5 StartZ=0 EndX=32.5 EndY=57.5 EndZ=0
    g3: LineSegment StartX=32.5 StartY=57.5 StartZ=0 EndX=12.5 EndY=57.5 EndZ=0
  constraints (10):
    c: Coincident(g0,g1)
    c: Coincident(g1,g2)
    c: Coincident(g2,g3)
    c: Coincident(g3,g0)
    c: Vertical(g0)
    c: Horizontal(g1)
    c: DistanceX(g3,g3) = 20
    c: DistanceY(g2,g2) = 25
    c: Tangent(g2,g-4)
    c: Tangent(g3,g-3)
FEATURE [PartDesign::Pocket] Pocket043  label="Frame rebate opening top005"
  BaseFeature = -> Pocket042
  Direction = (-1,0,0)
  Length = 5
  Length2 = 5
  Placement = pos=(0,-32.5,7.2e-15) rot=(1,0,0;1.5708rad)
  Profile = -> Sketch049
  ReferenceAxis = -> Sketch049 [N_Axis]
  Refine = true
  Suppressed = false
  Type = 1
FEATURE [Sketcher::SketchObject] Sketch050
  ArcFitTolerance = 0
  AttachmentSupport = -> [DatumPlane029]
  ExternalGeometry = -> [DatumPlane034,DatumPlane028]
  FullyConstrained = true
  MakeInternals = false
  MapMode = 5
  Placement = pos=(305,0,0) rot=(0.57735,0.57735,0.57735;2.0944rad)
  expr: Constraints[6] = <<Parameters>>.WindowInnerLipWidth
  expr: Constraints[7] = <<Parameters>>.FrameThickness
  sketch-geometry (4):
    g0: LineSegment StartX=32.5 StartY=57.5 StartZ=0 EndX=-17.5 EndY=57.5 EndZ=0
    g1: LineSegment StartX=-17.5 StartY=57.5 StartZ=0 EndX=-17.5 EndY=42.5 EndZ=0
    g2: LineSegment StartX=-17.5 StartY=42.5 StartZ=0 EndX=32.5 EndY=42.5 EndZ=0
    g3: LineSegment StartX=32.5 StartY=42.5 StartZ=0 EndX=32.5 EndY=57.5 EndZ=0
  constraints (10):
    c: Coincident(g0,g1)
    c: Coincident(g1,g2)
    c: Coincident(g2,g3)
    c: Coincident(g3,g0)
    c: Horizontal(g2)
    c: Vertical(g1)
    c: DistanceY(g3,g3) = 15
    c: DistanceX(g0,g0) = 50
    c: Tangent(g0,g-4)
    c: Tangent(g3,g-3)
FEATURE [PartDesign::Pocket] Pocket044  label="Frame rebate lip top004"
  BaseFeature = -> Pocket043
  Direction = (-1,0,0)
  Length = 5
  Length2 = 5
  Placement = pos=(0,-32.5,7.2e-15) rot=(1,0,0;1.5708rad)
  Profile = -> Sketch050
  ReferenceAxis = -> Sketch050 [N_Axis]
  Refine = true
  Suppressed = false
  Type = 1
FEATURE [Sketcher::SketchObject] Sketch051
  ArcFitTolerance = 0
  AttachmentSupport = -> [DatumPlane028]
  ExternalGeometry = -> [DatumPlane034,DatumPlane032]
  FullyConstrained = true
  MakeInternals = false
  MapMode = 5
  Placement = pos=(0,0,57.5) rot=(0,0,1;0rad)
  expr: Constraints[6] = <<Parameters>>.WindowInnerLipWidth
  expr: Constraints[7] = <<Parameters>>.WindowThickness
  sketch-geometry (4):
    g0: LineSegment StartX=-305 StartY=32.5 StartZ=0 EndX=-305 EndY=-32.5 EndZ=0
    g1: LineSegment StartX=-305 StartY=-32.5 StartZ=0 EndX=-290 EndY=-32.5 EndZ=0
    g2: LineSegment StartX=-290 StartY=-32.5 StartZ=0 EndX=-290 EndY=32.5 EndZ=0
    g3: LineSegment StartX=-290 StartY=32.5 StartZ=0 EndX=-305 EndY=32.5 EndZ=0
  constraints (10):
    c: Coincident(g0,g1)
    c: Coincident(g1,g2)
    c: Coincident(g2,g3)
    c: Coincident(g3,g0)
    c: Vertical(g2)
    c: Horizontal(g1)
    c: DistanceX(g3,g3) = 15
    c: DistanceY(g0,g0) = 65
    c: Tangent(g3,g-3)
    c: Tangent(g0,g-4)
FEATURE [Sketcher::SketchObject] Sketch052
  ArcFitTolerance = 0
  AttachmentSupport = -> [DatumPlane028]
  ExternalGeometry = -> [DatumPlane029,DatumPlane031]
  FullyConstrained = true
  MakeInternals = false
  MapMode = 5
  Placement = pos=(0,0,57.5) rot=(0,0,1;0rad)
  expr: Constraints[6] = <<Parameters>>.IntersectionRebateDepth
  expr: Constraints[7] = <<Parameters>>.IntersectionRebateWidth
  sketch-geometry (4):
    g0: LineSegment StartX=305 StartY=-5.68e-14 StartZ=0 EndX=295 EndY=-5.68e-14 EndZ=0
    g1: LineSegment StartX=295 StartY=-5.68e-14 StartZ=0 EndX=295 EndY=-32.5 EndZ=0
    g2: LineSegment StartX=295 StartY=-32.5 StartZ=0 EndX=305 EndY=-32.5 EndZ=0
    g3: LineSegment StartX=305 StartY=-32.5 StartZ=0 EndX=305 EndY=-5.68e-14 EndZ=0
  constraints (10):
    c: Coincident(g0,g1)
    c: Coincident(g1,g2)
    c: Coincident(g2,g3)
    c: Coincident(g3,g0)
    c: Horizontal(g0)
    c: Vertical(g1)
    c: DistanceX(g2,g2) = 10
    c: DistanceY(g3,g3) = 32.5
    c: Tangent(g2,g-4)
    c: Tangent(g3,g-3)
FEATURE [PartDesign::Pocket] Pocket045  label="Frame rebate lip left"
  BaseFeature = -> Pocket044
  Direction = (0,0,-1)
  Length = 5
  Length2 = 5
  Placement = pos=(0,-32.5,7.2e-15) rot=(1,0,0;1.5708rad)
  Profile = -> Sketch051
  ReferenceAxis = -> Sketch051 [N_Axis]
  Refine = true
  Suppressed = false
  Type = 1
FEATURE [PartDesign::Pocket] Pocket046  label="Frame rebate intersection right"
  BaseFeature = -> Pocket045
  Direction = (0,0,-1)
  Length = 5
  Length2 = 5
  Placement = pos=(0,-32.5,7.2e-15) rot=(1,0,0;1.5708rad)
  Profile = -> Sketch052
  ReferenceAxis = -> Sketch052 [N_Axis]
  Refine = true
  Suppressed = false
  Type = 1
FEATURE [PartDesign::Body] Body009  label="Rail top left"
  AllowCompound = false
  Group = -> [DatumPlane028,DatumPlane029,DatumPlane031,DatumPlane032,DatumPlane033,DatumPlane034,Sketch042,Pad004,Sketch043,Pocket037,Sketch044,Pocket038,Sketch045,Pocket039,Sketch046,Pocket040,Sketch047,Pocket041,Sketch048,Pocket042,Sketch049,Pocket043,Sketch050,Pocket044,Sketch051,Sketch052,Pocket045,Pocket046]
  Origin = -> Origin009
  Tip = -> Pocket046
COMPONENT P12 — recipe-attached ("Rail top right001", modeled in this document).
Construction recipe (the document's own serialized feature program — sketch geometry with constraints, then the solid features built on it; lengths are millimeters unless a unit is written):

FEATURE [PartDesign::FeatureBase] BaseFeature005
  BaseFeature = -> Part__Mirroring004
  Suppressed = false
FEATURE [PartDesign::Body] Body011  label="Rail top right"
  AllowCompound = false
  BaseFeature = -> Part__Mirroring004
  Group = -> [BaseFeature005]
  Origin = -> Origin011
  Tip = -> BaseFeature005
COMPONENT P13 — recipe-attached ("Stile inner left002", modeled in this document).
Construction recipe (the document's own serialized feature program — sketch geometry with constraints, then the solid features built on it; lengths are millimeters unless a unit is written):

FEATURE [PartDesign::Plane] DatumPlane008  label="DatumPlane top002"
  AttachmentOffset = pos=(0,0,935) rot=(0,0,1;0rad)
  AttachmentSupport = -> [X_Axis003]
  Length = 70
  MapMode = 2
  Placement = pos=(0,0,935) rot=(0,0,1;0rad)
  ResizeMode = 1
  Width = 65
  expr: .AttachmentOffset.Base.z = <<Parameters>>.StileLength / 2
  expr: Length = <<Parameters>>.StileInnerWidth
  expr: Width = <<Parameters>>.WindowThickness
FEATURE [PartDesign::Plane] DatumPlane009  label="DatumPlane right002"
  AttachmentOffset = pos=(0,0,35) rot=(0,0,1;0rad)
  AttachmentSupport = -> [X_Axis003]
  Length = 65
  MapMode = 4
  Placement = pos=(35,0,0) rot=(0.57735,0.57735,0.57735;2.0944rad)
  ResizeMode = 1
  Width = 1870
  expr: .AttachmentOffset.Base.z = <<Parameters>>.StileInnerWidth / 2
  expr: Length = <<Parameters>>.WindowThickness
  expr: Width = <<Parameters>>.StileLength
FEATURE [PartDesign::Plane] DatumPlane010  label="DatumPlane rear001"
  AttachmentOffset = pos=(0,0,32.5) rot=(0,0,1;0rad)
  AttachmentSupport = -> [X_Axis003]
  Length = 70
  MapMode = 3
  Placement = pos=(0,32.5,-7.2e-15) rot=(0,0.707107,0.707107;3.14159rad)
  ResizeMode = 1
  Width = 1870
  expr: .AttachmentOffset.Base.z = <<Parameters>>.WindowThickness / 2
  expr: Length = <<Parameters>>.StileInnerWidth
  expr: Width = <<Parameters>>.StileLength
FEATURE [PartDesign::Plane] DatumPlane011  label="DatumPlane bottom001"
  AttachmentOffset = pos=(0,0,935) rot=(0,0,1;0rad)
  AttachmentSupport = -> [X_Axis003]
  Length = 70
  MapMode = 2
  Placement = pos=(0,0,-935) rot=(0,1,0;3.14159rad)
  ResizeMode = 1
  Width = 65
  expr: .AttachmentOffset.Base.z = <<Parameters>>.StileLength / 2
  expr: Length = <<Parameters>>.StileInnerWidth
  expr: Width = <<Parameters>>.WindowThickness
FEATURE [PartDesign::Plane] DatumPlane012  label="DatumPlane left001"
  AttachmentOffset = pos=(0,0,35) rot=(0,0,1;0rad)
  AttachmentSupport = -> [X_Axis003]
  Length = 65
  MapMode = 4
  Placement = pos=(-35,0,0) rot=(0.57735,-0.57735,-0.57735;2.0944rad)
  ResizeMode = 1
  Width = 1870
  expr: .AttachmentOffset.Base.z = <<Parameters>>.StileInnerWidth / 2
  expr: Length = <<Parameters>>.WindowThickness
  expr: Width = <<Parameters>>.StileLength
FEATURE [Sketcher::SketchObject] Sketch022
  ArcFitTolerance = 0
  AttachmentSupport = -> [DatumPlane008]
  FullyConstrained = true
  MakeInternals = false
  MapMode = 5
  Placement = pos=(0,0,935) rot=(0,0,1;0rad)
  expr: Constraints[10] = <<Parameters>>.StileInnerWidth
  expr: Constraints[11] = <<Parameters>>.WindowThickness
  sketch-geometry (5):
    g0: LineSegment StartX=-35 StartY=32.5 StartZ=0 EndX=-35 EndY=-32.5 EndZ=0
    g1: LineSegment StartX=-35 StartY=-32.5 StartZ=0 EndX=35 EndY=-32.5 EndZ=0
    g2: LineSegment StartX=35 StartY=-32.5 StartZ=0 EndX=35 EndY=32.5 EndZ=0
    g3: LineSegment StartX=35 StartY=32.5 StartZ=0 EndX=-35 EndY=32.5 EndZ=0
    g4: GeomPoint [constr] X=0 Y=0 Z=0
  constraints (12):
    c: Coincident(g0,g1)
    c: Coincident(g1,g2)
    c: Coincident(g2,g3)
    c: Coincident(g3,g0)
    c: Vertical(g0)
    c: Vertical(g2)
    c: Horizontal(g1)
    c: Horizontal(g3)
    c: Symmetric(g2,g0,g4)
    c: Coincident(g4,g-1)
    c: DistanceX(g3,g3) = 70
    c: DistanceY(g0,g0) = 65
FEATURE [PartDesign::Pad] Pad002  label="Stock002"
  Direction = (0,0,1)
  Length = 1870
  Length2 = 10
  Placement = pos=(0,0,935) rot=(0,0,1;0rad)
  Profile = -> Sketch022
  ReferenceAxis = -> Sketch022 [N_Axis]
  Refine = true
  Reversed = true
  Suppressed = false
  Type = 0
  expr: Length = <<Parameters>>.StileLength
FEATURE [Sketcher::SketchObject] Sketch023
  ArcFitTolerance = 0
  AttachmentSupport = -> [DatumPlane009]
  ExternalGeometry = -> [DatumPlane010,DatumPlane011]
  FullyConstrained = true
  MakeInternals = false
  MapMode = 5
  Placement = pos=(35,0,0) rot=(0.57735,0.57735,0.57735;2.0944rad)
  expr: Constraints[30] = <<Parameters>>.GlassOpeningHeigth
  expr: Constraints[31] = <<Parameters>>.GlassOpeningHeigth
  expr: Constraints[32] = <<Parameters>>.MuntinTenonThickness
  expr: Constraints[33] = <<Parameters>>.GlassRebateDepth
  expr: Constraints[34] = <<Parameters>>.GlassOpeningHeigth + <<Parameters>>.RailBottomWidth
  expr: Constraints[8] = <<Parameters>>.MuntinWidth
  sketch-geometry (12):
    g0: LineSegment StartX=-9.5 StartY=-290 StartZ=0 EndX=-9.5 EndY=-320 EndZ=0
    g1: LineSegment StartX=-9.5 StartY=-320 StartZ=0 EndX=0.5 EndY=-320 EndZ=0
    g2: LineSegment StartX=0.5 StartY=-320 StartZ=0 EndX=0.5 EndY=-290 EndZ=0
    g3: LineSegment StartX=0.5 StartY=-290 StartZ=0 EndX=-9.5 EndY=-290 EndZ=0
    g4: LineSegment StartX=-9.5 StartY=160 StartZ=0 EndX=-9.5 EndY=190 EndZ=0
    g5: LineSegment StartX=-9.5 StartY=190 StartZ=0 EndX=0.5 EndY=190 EndZ=0
    g6: LineSegment StartX=0.5 StartY=190 StartZ=0 EndX=0.5 EndY=160 EndZ=0
    g7: LineSegment StartX=0.5 StartY=160 StartZ=0 EndX=-9.5 EndY=160 EndZ=0
    g8: LineSegment StartX=-9.5 StartY=670 StartZ=0 EndX=-9.5 EndY=640 EndZ=0
    g9: LineSegment StartX=-9.5 StartY=640 StartZ=0 EndX=0.5 EndY=640 EndZ=0
    g10: LineSegment StartX=0.5 StartY=640 StartZ=0 EndX=0.5 EndY=670 EndZ=0
    g11: LineSegment StartX=0.5 StartY=670 StartZ=0 EndX=-9.5 EndY=670 EndZ=0
  constraints (36):
    c: Coincident(g0,g1)
    c: Coincident(g1,g2)
    c: Coincident(g2,g3)
    c: Coincident(g3,g0)
    c: Vertical(g0)
    c: Vertical(g2)
    c: Horizontal(g1)
    c: Horizontal(g3)
    c: DistanceY(g0,g0) = 30
    c: Coincident(g4,g5)
    c: Coincident(g8,g9)
    c: Coincident(g5,g6)
    c: Coincident(g9,g10)
    c: Coincident(g6,g7)
    c: Coincident(g10,g11)
    c: Coincident(g7,g4)
    c: Coincident(g11,g8)
    c: Vertical(g4)
    c: Vertical(g8)
    c: Vertical(g6)
    c: Vertical(g10)
    c: Horizontal(g5)
    c: Horizontal(g9)
    c: Horizontal(g7)
    c: Horizontal(g11)
    c: Equal(g0,g4)
    c: Equal(g0,g8)
    c: Equal(g11,g7)
    c: Equal(g7,g3)
    c: Vertical(g5,g9)
    c: DistanceY(g0,g4) = 450
    c: DistanceY(g4,g8) = 450
    c: DistanceX(g1,g1) = 10
    c: Distance(g1,g-3) = 32
    c: Distance(g0,g-4) = 615
    c: Vertical(g6,g2)
FEATURE [Sketcher::SketchObject] Sketch024  label="Frame rebate opening top004"
  ArcFitTolerance = 0
  AttachmentSupport = -> [DatumPlane009]
  ExternalGeometry = -> [DatumPlane008,DatumPlane010]
  FullyConstrained = true
  MakeInternals = false
  MapMode = 5
  Placement = pos=(35,0,0) rot=(0.57735,0.57735,0.57735;2.0944rad)
  expr: Constraints[6] = <<Parameters>>.WindowFrameRebateWidth
  expr: Constraints[7] = <<Parameters>>.WindowFrameRebateDepth
  sketch-geometry (4):
    g0: LineSegment StartX=12.5 StartY=935 StartZ=0 EndX=12.5 EndY=910 EndZ=0
    g1: LineSegment StartX=12.5 StartY=910 StartZ=0 EndX=32.5 EndY=910 EndZ=0
    g2: LineSegment StartX=32.5 StartY=910 StartZ=0 EndX=32.5 EndY=935 EndZ=0
    g3: LineSegment StartX=32.5 StartY=935 StartZ=0 EndX=12.5 EndY=935 EndZ=0
  constraints (10):
    c: Coincident(g0,g1)
    c: Coincident(g1,g2)
    c: Coincident(g2,g3)
    c: Coincident(g3,g0)
    c: Vertical(g0)
    c: Horizontal(g1)
    c: DistanceX(g3,g3) = 20
    c: Distance(g2,g2) = 25
    c: Tangent(g2,g-4)
    c: Tangent(g3,g-3)
FEATURE [Sketcher::SketchObject] Sketch025  label="Frame rebate closure top004"
  ArcFitTolerance = 0
  AttachmentSupport = -> [DatumPlane009]
  ExternalGeometry = -> [DatumPlane008,DatumPlane010]
  FullyConstrained = true
  MakeInternals = false
  MapMode = 5
  Placement = pos=(35,0,0) rot=(0.57735,0.57735,0.57735;2.0944rad)
  expr: Constraints[6] = <<Parameters>>.WindowInnerLipWidth
  expr: Constraints[7] = <<Parameters>>.FrameThickness
  sketch-geometry (4):
    g0: LineSegment StartX=-17.5 StartY=935 StartZ=0 EndX=-17.5 EndY=920 EndZ=0
    g1: LineSegment StartX=-17.5 StartY=920 StartZ=0 EndX=32.5 EndY=920 EndZ=0
    g2: LineSegment StartX=32.5 StartY=920 StartZ=0 EndX=32.5 EndY=935 EndZ=0
    g3: LineSegment StartX=32.5 StartY=935 StartZ=0 EndX=-17.5 EndY=935 EndZ=0
  constraints (10):
    c: Coincident(g0,g1)
    c: Coincident(g1,g2)
    c: Coincident(g2,g3)
    c: Coincident(g3,g0)
    c: Vertical(g0)
    c: Horizontal(g1)
    c: DistanceY(g2,g2) = 15
    c: DistanceX(g3,g3) = 50
    c: Tangent(g3,g-3)
    c: Tangent(g-4,g2)
FEATURE [Sketcher::SketchObject] Sketch026  label="Frame rebate opening right"
  ArcFitTolerance = 0
  AttachmentSupport = -> [DatumPlane008]
  ExternalGeometry = -> [DatumPlane010,DatumPlane012]
  FullyConstrained = true
  MakeInternals = false
  MapMode = 5
  Placement = pos=(0,0,935) rot=(0,0,1;0rad)
  expr: Constraints[6] = <<Parameters>>.WindowFrameRebateDepth
  expr: Constraints[7] = <<Parameters>>.WindowFrameRebateWidth
  sketch-geometry (4):
    g0: LineSegment StartX=-35 StartY=32.5 StartZ=0 EndX=-35 EndY=12.5 EndZ=0
    g1: LineSegment StartX=-35 StartY=12.5 StartZ=0 EndX=-10 EndY=12.5 EndZ=0
    g2: LineSegment StartX=-10 StartY=12.5 StartZ=0 EndX=-10 EndY=32.5 EndZ=0
    g3: LineSegment StartX=-10 StartY=32.5 StartZ=0 EndX=-35 EndY=32.5 EndZ=0
  constraints (10):
    c: Coincident(g0,g1)
    c: Coincident(g1,g2)
    c: Coincident(g2,g3)
    c: Coincident(g3,g0)
    c: Vertical(g2)
    c: Horizontal(g1)
    c: DistanceX(g3,g3) = 25
    c: DistanceY(g0,g0) = 20
    c: Tangent(g3,g-3)
    c: Tangent(g0,g-4)
FEATURE [Sketcher::SketchObject] Sketch027  label="Frame rebate lip right004"
  ArcFitTolerance = 0
  AttachmentSupport = -> [DatumPlane008]
  ExternalGeometry = -> [DatumPlane010,DatumPlane012]
  FullyConstrained = true
  MakeInternals = false
  MapMode = 5
  Placement = pos=(0,0,935) rot=(0,0,1;0rad)
  expr: Constraints[6] = <<Parameters>>.WindowInnerLipWidth
  expr: Constraints[7] = <<Parameters>>.FrameThickness
  sketch-geometry (4):
    g0: LineSegment StartX=-35 StartY=32.5 StartZ=0 EndX=-35 EndY=-17.5 EndZ=0
    g1: LineSegment StartX=-35 StartY=-17.5 StartZ=0 EndX=-20 EndY=-17.5 EndZ=0
    g2: LineSegment StartX=-20 StartY=-17.5 StartZ=0 EndX=-20 EndY=32.5 EndZ=0
    g3: LineSegment StartX=-20 StartY=32.5 StartZ=0 EndX=-35 EndY=32.5 EndZ=0
  constraints (10):
    c: Coincident(g0,g1)
    c: Coincident(g1,g2)
    c: Coincident(g2,g3)
    c: Coincident(g3,g0)
    c: Vertical(g2)
    c: Horizontal(g1)
    c: DistanceX(g3,g3) = 15
    c: DistanceY(g0,g0) = 50
    c: Tangent(g3,g-3)
    c: Tangent(g0,g-4)
FEATURE [Sketcher::SketchObject] Sketch028  label="Mortise rail top005"
  ArcFitTolerance = 0
  AttachmentOffset = pos=(0,0,-32) rot=(0,0,1;0rad)
  AttachmentSupport = -> [DatumPlane010]
  ExternalGeometry = -> [DatumPlane012,DatumPlane008]
  FullyConstrained = true
  MakeInternals = false
  MapMode = 5
  Placement = pos=(0,0.5,-1e-16) rot=(0,0.707107,0.707107;3.14159rad)
  expr: .AttachmentOffset.Base.z = -<<Parameters>>.GlassRebateDepth
  expr: Constraints[10] = <<Parameters>>.RailTopWidth
  expr: Constraints[11] = <<Parameters>>.RailTopTenonWidth
  expr: Constraints[13] = <<Parameters>>.StileInnerHaunchDepth
  expr: Constraints[9] = <<Parameters>>.StileInnerWidth
  sketch-geometry (6):
    g0: LineSegment StartX=-35 StartY=890 StartZ=0 EndX=15 EndY=890 EndZ=0
    g1: LineSegment StartX=15 StartY=890 StartZ=0 EndX=15 EndY=935 EndZ=0
    g2: LineSegment StartX=15 StartY=935 StartZ=0 EndX=35 EndY=935 EndZ=0
    g3: LineSegment StartX=35 StartY=935 StartZ=0 EndX=35 EndY=820 EndZ=0
    g4: LineSegment StartX=35 StartY=820 StartZ=0 EndX=-35 EndY=820 EndZ=0
    g5: LineSegment StartX=-35 StartY=820 StartZ=0 EndX=-35 EndY=890 EndZ=0
  constraints (16):
    c: Coincident(g0,g1)
    c: Vertical(g1)
    c: Coincident(g1,g2)
    c: Coincident(g2,g3)
    c: Coincident(g3,g4)
    c: Horizontal(g4)
    c: Coincident(g4,g5)
    c: Coincident(g5,g0)
    c: Vertical(g5)
    c: DistanceX(g4,g4) = 70
    c: DistanceY(g3,g3) = 115
    c: DistanceY(g5,g5) = 70
    c: Tangent(g-3,g3)
    c: DistanceX(g2,g2) = 20
    c: Horizontal(g0,g0)
    c: Tangent(g2,g-4)
FEATURE [PartDesign::Pocket] Pocket024  label="Mortise rail top004"
  BaseFeature = -> Pad002
  Direction = (0,-1,2e-16)
  Length = 15
  Length2 = 5
  Placement = pos=(0,0,935) rot=(0,0,1;0rad)
  Profile = -> Sketch028
  ReferenceAxis = -> Sketch028 [N_Axis]
  Refine = true
  Suppressed = false
  Type = 0
  expr: Length = <<Parameters>>.RailTenonThickness
FEATURE [Sketcher::SketchObject] Sketch029
  ArcFitTolerance = 0
  AttachmentSupport = -> [DatumPlane008]
  ExternalGeometry = -> [DatumPlane010,DatumPlane012]
  FullyConstrained = true
  MakeInternals = false
  MapMode = 5
  Placement = pos=(0,0,935) rot=(0,0,1;0rad)
  expr: Constraints[5] = <<Parameters>>.GlassRebateDepth
  expr: Constraints[6] = <<Parameters>>.GlassRebateWidth
  sketch-geometry (4):
    g0: LineSegment StartX=-35 StartY=32.5 StartZ=0 EndX=-35 EndY=0.5 EndZ=0
    g1: LineSegment StartX=-35 StartY=0.5 StartZ=0 EndX=-25 EndY=0.5 EndZ=0
    g2: LineSegment StartX=-25 StartY=0.5 StartZ=0 EndX=-25 EndY=32.5 EndZ=0
    g3: LineSegment StartX=-25 StartY=32.5 StartZ=0 EndX=-35 EndY=32.5 EndZ=0
  constraints (10):
    c: Coincident(g0,g1)
    c: Coincident(g1,g2)
    c: Coincident(g2,g3)
    c: Coincident(g3,g0)
    c: Horizontal(g1)
    c: DistanceY(g2,g2) = 32
    c: DistanceX(g3,g3) = 10
    c: Tangent(g3,g-3)
    c: Vertical(g1,g2)
    c: Tangent(g0,g-4)
FEATURE [Sketcher::SketchObject] Sketch030
  ArcFitTolerance = 0
  AttachmentOffset = pos=(0,0,-32) rot=(0,0,1;0rad)
  AttachmentSupport = -> [DatumPlane010]
  ExternalGeometry = -> [DatumPlane011,DatumPlane009]
  FullyConstrained = true
  MakeInternals = false
  MapMode = 5
  Placement = pos=(0,0.5,-1e-16) rot=(0,0.707107,0.707107;3.14159rad)
  expr: .AttachmentOffset.Base.z = -<<Parameters>>.GlassRebateDepth
  expr: Constraints[10] = <<Parameters>>.RailBottomWidth
  expr: Constraints[11] = <<Parameters>>.RailBottomTenonWidth
  expr: Constraints[14] = <<Parameters>>.StileInnerHaunchDepth
  expr: Constraints[9] = <<Parameters>>.StileInnerWidth
  sketch-geometry (6):
    g0: LineSegment StartX=35 StartY=-770 StartZ=0 EndX=-35 EndY=-770 EndZ=0
    g1: LineSegment StartX=-35 StartY=-770 StartZ=0 EndX=-35 EndY=-870 EndZ=0
    g2: LineSegment StartX=-35 StartY=-870 StartZ=0 EndX=15 EndY=-870 EndZ=0
    g3: LineSegment StartX=15 StartY=-870 StartZ=0 EndX=15 EndY=-935 EndZ=0
    g4: LineSegment StartX=15 StartY=-935 StartZ=0 EndX=35 EndY=-935 EndZ=0
    g5: LineSegment StartX=35 StartY=-935 StartZ=0 EndX=35 EndY=-770 EndZ=0
  constraints (16):
    c: Horizontal(g0)
    c: Coincident(g0,g1)
    c: Coincident(g1,g2)
    c: Coincident(g2,g3)
    c: Vertical(g3)
    c: Coincident(g3,g4)
    c: Coincident(g4,g5)
    c: Coincident(g5,g0)
    c: Vertical(g5)
    c: DistanceX(g0,g0) = 70
    c: DistanceY(g5,g5) = 165
    c: DistanceY(g1,g1) = 100
    c: Tangent(g1,g-4)
    c: Horizontal(g2,g1)
    c: DistanceX(g4,g4) = 20
    c: Tangent(g4,g-3)
FEATURE [PartDesign::Pocket] Pocket026  label="Mortise rail bottom003"
  BaseFeature = -> Pocket024
  Direction = (0,-1,2e-16)
  Length = 15
  Length2 = 5
  Placement = pos=(0,0,935) rot=(0,0,1;0rad)
  Profile = -> Sketch030
  ReferenceAxis = -> Sketch030 [N_Axis]
  Refine = true
  Suppressed = false
  Type = 0
  expr: Length = <<Parameters>>.RailTenonThickness
FEATURE [PartDesign::Pocket] Pocket019  label="Mortises muntin001"
  BaseFeature = -> Pocket026
  Direction = (-1,0,0)
  Length = 5
  Length2 = 5
  Placement = pos=(0,0,935) rot=(0,0,1;0rad)
  Profile = -> Sketch023
  ReferenceAxis = -> Sketch023 [N_Axis]
  Refine = true
  Suppressed = false
  Type = 1
FEATURE [PartDesign::Pocket] Pocket020  label="Frame rebate opening top003"
  BaseFeature = -> Pocket019
  Direction = (-1,0,0)
  Length = 5
  Length2 = 5
  Placement = pos=(0,0,935) rot=(0,0,1;0rad)
  Profile = -> Sketch024
  ReferenceAxis = -> Sketch024 [N_Axis]
  Refine = true
  Suppressed = false
  Type = 1
FEATURE [PartDesign::Pocket] Pocket021  label="Frame rebate lip top003"
  BaseFeature = -> Pocket020
  Direction = (-1,0,0)
  Length = 5
  Length2 = 5
  Placement = pos=(0,0,935) rot=(0,0,1;0rad)
  Profile = -> Sketch025
  ReferenceAxis = -> Sketch025 [N_Axis]
  Refine = true
  Suppressed = false
  Type = 1
FEATURE [PartDesign::Mirrored] Mirrored003  label="Frame rebates bottom001"
  BaseFeature = -> Pocket021
  MirrorPlane = -> XY_Plane003
  Originals = -> [Pocket020,Pocket021]
  Placement = pos=(0,0,935) rot=(0,0,1;0rad)
  Refine = true
  Suppressed = false
  TransformMode = 0
FEATURE [PartDesign::Pocket] Pocket025  label="Glass rebate001"
  BaseFeature = -> Mirrored003
  Direction = (0,0,-1)
  Length = 5
  Length2 = 5
  Placement = pos=(0,0,935) rot=(0,0,1;0rad)
  Profile = -> Sketch029
  ReferenceAxis = -> Sketch029 [N_Axis]
  Refine = true
  Suppressed = false
  Type = 1
FEATURE [PartDesign::Plane] DatumPlane013  label="DatumPlane front001"
  AttachmentOffset = pos=(0,0,32.5) rot=(0,0,1;0rad)
  AttachmentSupport = -> [X_Axis003]
  Length = 70
  MapMode = 3
  Placement = pos=(0,-32.5,7.2e-15) rot=(1,0,0;1.5708rad)
  ResizeMode = 1
  Width = 1870
  expr: .AttachmentOffset.Base.z = <<Parameters>>.WindowThickness / 2
  expr: Length = <<Parameters>>.StileInnerWidth
  expr: Width = <<Parameters>>.StileLength
FEATURE [Sketcher::SketchObject] Sketch031
  ArcFitTolerance = 0
  AttachmentSupport = -> [DatumPlane008]
  ExternalGeometry = -> [DatumPlane009,DatumPlane013]
  FullyConstrained = true
  MakeInternals = false
  MapMode = 5
  Placement = pos=(0,0,935) rot=(0,0,1;0rad)
  expr: Constraints[6] = <<Parameters>>.IntersectionRebateWidth
  expr: Constraints[7] = <<Parameters>>.IntersectionRebateDepth
  sketch-geometry (4):
    g0: LineSegment StartX=25 StartY=-7.1e-15 StartZ=0 EndX=25 EndY=-32.5 EndZ=0
    g1: LineSegment StartX=25 StartY=-32.5 StartZ=0 EndX=35 EndY=-32.5 EndZ=0
    g2: LineSegment StartX=35 StartY=-32.5 StartZ=0 EndX=35 EndY=-7.1e-15 EndZ=0
    g3: LineSegment StartX=35 StartY=-7.1e-15 StartZ=0 EndX=25 EndY=-7.1e-15 EndZ=0
  constraints (10):
    c: Coincident(g0,g1)
    c: Coincident(g1,g2)
    c: Coincident(g2,g3)
    c: Coincident(g3,g0)
    c: Vertical(g0)
    c: Horizontal(g3)
    c: DistanceY(g2,g2) = 32.5
    c: Distance(g1,g1) = 10
    c: Tangent(g2,g-3)
    c: Tangent(g1,g-4)
FEATURE [PartDesign::Pocket] Pocket027  label="Rebate intersection left"
  BaseFeature = -> Pocket025
  Direction = (0,0,-1)
  Length = 5
  Length2 = 5
  Placement = pos=(0,0,935) rot=(0,0,1;0rad)
  Profile = -> Sketch031
  ReferenceAxis = -> Sketch031 [N_Axis]
  Refine = true
  Suppressed = false
  Type = 1
FEATURE [PartDesign::Body] Body003  label="Stile inner left"
  AllowCompound = false
  Group = -> [DatumPlane008,DatumPlane009,DatumPlane010,DatumPlane011,DatumPlane012,DatumPlane013,Sketch022,Pad002,Pocket024,Pocket026,Sketch023,Pocket019,Sketch024,Pocket020,Sketch025,Pocket021,Mirrored003,Sketch026,Sketch027,Sketch028,Sketch029,Pocket025,Sketch030,Sketch031,Pocket027]
  Origin = -> Origin003
  Tip = -> Pocket027
COMPONENT P14 — recipe-attached ("Stile inner right001", modeled in this document).
Construction recipe (the document's own serialized feature program — sketch geometry with constraints, then the solid features built on it; lengths are millimeters unless a unit is written):

FEATURE [PartDesign::FeatureBase] BaseFeature001
  BaseFeature = -> Part__Mirroring001
  Suppressed = false
FEATURE [PartDesign::Plane] DatumPlane014  label="DatumPlane top003"
  AttachmentOffset = pos=(0,0,935) rot=(0,0,1;0rad)
  AttachmentSupport = -> [X_Axis004]
  Length = 70
  MapMode = 2
  Placement = pos=(0,0,935) rot=(0,0,1;0rad)
  ResizeMode = 1
  Width = 65
  expr: .AttachmentOffset.Base.z = <<Parameters>>.StileLength / 2
  expr: Length = <<Parameters>>.StileInnerWidth
  expr: Width = <<Parameters>>.WindowThickness
FEATURE [PartDesign::Plane] DatumPlane016  label="DatumPlane rear002"
  AttachmentOffset = pos=(0,0,32.5) rot=(0,0,1;0rad)
  AttachmentSupport = -> [X_Axis004]
  Length = 70
  MapMode = 3
  Placement = pos=(0,32.5,-7.2e-15) rot=(0,0.707107,0.707107;3.14159rad)
  ResizeMode = 1
  Width = 1870
  expr: .AttachmentOffset.Base.z = <<Parameters>>.WindowThickness / 2
  expr: Length = <<Parameters>>.StileInnerWidth
  expr: Width = <<Parameters>>.StileLength
FEATURE [PartDesign::Plane] DatumPlane017  label="DatumPlane left002"
  AttachmentOffset = pos=(0,0,35) rot=(0,0,1;0rad)
  AttachmentSupport = -> [X_Axis004]
  Length = 65
  MapMode = 4
  Placement = pos=(-35,0,0) rot=(0.57735,-0.57735,-0.57735;2.0944rad)
  ResizeMode = 1
  Width = 1870
  expr: .AttachmentOffset.Base.z = <<Parameters>>.StileInnerWidth / 2
  expr: Length = <<Parameters>>.WindowThickness
  expr: Width = <<Parameters>>.StileLength
FEATURE [Sketcher::SketchObject] Sketch032
  ArcFitTolerance = 0
  AttachmentSupport = -> [DatumPlane014]
  ExternalGeometry = -> [DatumPlane016,DatumPlane017]
  FullyConstrained = true
  MakeInternals = false
  MapMode = 5
  Placement = pos=(0,0,935) rot=(0,0,1;0rad)
  expr: Constraints[6] = <<Parameters>>.IntersectionRebateDepth
  expr: Constraints[7] = <<Parameters>>.IntersectionRebateWidth
  sketch-geometry (4):
    g0: LineSegment StartX=-35 StartY=32.5 StartZ=0 EndX=-35 EndY=0 EndZ=0
    g1: LineSegment StartX=-35 StartY=0 StartZ=0 EndX=-25 EndY=0 EndZ=0
    g2: LineSegment StartX=-25 StartY=0 StartZ=0 EndX=-25 EndY=32.5 EndZ=0
    g3: LineSegment StartX=-25 StartY=32.5 StartZ=0 EndX=-35 EndY=32.5 EndZ=0
  constraints (10):
    c: Coincident(g0,g1)
    c: Coincident(g1,g2)
    c: Coincident(g2,g3)
    c: Coincident(g3,g0)
    c: Vertical(g2)
    c: Horizontal(g1)
    c: DistanceX(g3,g3) = 10
    c: DistanceY(g0,g0) = 32.5
    c: Tangent(g0,g-4)
    c: Tangent(g3,g-3)
FEATURE [PartDesign::Pocket] Pocket028  label="Rebate intersection right"
  BaseFeature = -> BaseFeature001
  Direction = (0,0,-1)
  Length = 5
  Length2 = 5
  Profile = -> Sketch032
  ReferenceAxis = -> Sketch032 [N_Axis]
  Refine = true
  Suppressed = false
  Type = 1
FEATURE [PartDesign::Body] Body004  label="Stile inner right"
  AllowCompound = false
  BaseFeature = -> Part__Mirroring001
  Group = -> [BaseFeature001,DatumPlane014,DatumPlane016,DatumPlane017,Sketch032,Pocket028]
  Origin = -> Origin004
  Tip = -> Pocket028
COMPONENT P15 — recipe-attached ("Stile outer left001", modeled in this document).
Construction recipe (the document's own serialized feature program — sketch geometry with constraints, then the solid features built on it; lengths are millimeters unless a unit is written):

FEATURE [PartDesign::Plane] DatumPlane003  label="DatumPlane top001"
  AttachmentOffset = pos=(0,0,935) rot=(0,0,1;0rad)
  AttachmentSupport = -> [X_Axis001]
  Length = 90
  MapMode = 2
  Placement = pos=(0,0,935) rot=(0,0,1;0rad)
  ResizeMode = 1
  Width = 65
  expr: .AttachmentOffset.Base.z = <<Parameters>>.StileLength / 2
  expr: Length = <<Parameters>>.StileOuterWidth
  expr: Width = <<Parameters>>.WindowThickness
FEATURE [PartDesign::Plane] DatumPlane004  label="DatumPlane right001"
  AttachmentOffset = pos=(0,0,45) rot=(0,0,1;0rad)
  AttachmentSupport = -> [X_Axis001]
  Length = 65
  MapMode = 4
  Placement = pos=(45,0,0) rot=(0.57735,0.57735,0.57735;2.0944rad)
  ResizeMode = 1
  Width = 1870
  expr: .AttachmentOffset.Base.z = <<Parameters>>.StileOuterWidth / 2
  expr: Length = <<Parameters>>.WindowThickness
  expr: Width = <<Parameters>>.StileLength
FEATURE [PartDesign::Plane] DatumPlane005  label="DatumPlane rear"
  AttachmentOffset = pos=(0,0,32.5) rot=(0,0,1;0rad)
  AttachmentSupport = -> [X_Axis001]
  Length = 90
  MapMode = 3
  Placement = pos=(0,32.5,-7.2e-15) rot=(0,0.707107,0.707107;3.14159rad)
  ResizeMode = 1
  Width = 1870
  expr: .AttachmentOffset.Base.z = <<Parameters>>.WindowThickness / 2
  expr: Length = <<Parameters>>.StileOuterWidth
  expr: Width = <<Parameters>>.StileLength
FEATURE [Sketcher::SketchObject] Sketch003
  ArcFitTolerance = 0
  AttachmentSupport = -> [DatumPlane003]
  FullyConstrained = true
  MakeInternals = false
  MapMode = 5
  Placement = pos=(0,0,935) rot=(0,0,1;0rad)
  expr: Constraints[10] = <<Parameters>>.StileOuterWidth
  expr: Constraints[11] = <<Parameters>>.WindowThickness
  sketch-geometry (5):
    g0: LineSegment StartX=-45 StartY=32.5 StartZ=0 EndX=-45 EndY=-32.5 EndZ=0
    g1: LineSegment StartX=-45 StartY=-32.5 StartZ=0 EndX=45 EndY=-32.5 EndZ=0
    g2: LineSegment StartX=45 StartY=-32.5 StartZ=0 EndX=45 EndY=32.5 EndZ=0
    g3: LineSegment StartX=45 StartY=32.5 StartZ=0 EndX=-45 EndY=32.5 EndZ=0
    g4: GeomPoint [constr] X=0 Y=0 Z=0
  constraints (12):
    c: Coincident(g0,g1)
    c: Coincident(g1,g2)
    c: Coincident(g2,g3)
    c: Coincident(g3,g0)
    c: Vertical(g0)
    c: Vertical(g2)
    c: Horizontal(g1)
    c: Horizontal(g3)
    c: Symmetric(g2,g0,g4)
    c: Coincident(g4,g-1)
    c: DistanceX(g3,g3) = 90
    c: DistanceY(g0,g0) = 65
FEATURE [PartDesign::Pad] Pad001  label="Stock001"
  Direction = (0,0,1)
  Length = 1870
  Length2 = 10
  Placement = pos=(0,0,935) rot=(0,0,1;0rad)
  Profile = -> Sketch003
  ReferenceAxis = -> Sketch003 [N_Axis]
  Refine = true
  Reversed = true
  Suppressed = false
  Type = 0
  expr: Length = <<Parameters>>.StileLength
FEATURE [PartDesign::Plane] DatumPlane006  label="DatumPlane bottom"
  AttachmentOffset = pos=(0,0,935) rot=(0,0,1;0rad)
  AttachmentSupport = -> [X_Axis001]
  Length = 90
  MapMode = 2
  Placement = pos=(0,0,-935) rot=(0,1,0;3.14159rad)
  ResizeMode = 1
  Width = 65
  expr: .AttachmentOffset.Base.z = <<Parameters>>.StileLength / 2
  expr: Length = <<Parameters>>.StileOuterWidth
  expr: Width = <<Parameters>>.WindowThickness
FEATURE [Sketcher::SketchObject] Sketch006
  ArcFitTolerance = 0
  AttachmentSupport = -> [DatumPlane004]
  ExternalGeometry = -> [DatumPlane005,DatumPlane006]
  FullyConstrained = true
  MakeInternals = false
  MapMode = 5
  Placement = pos=(45,0,0) rot=(0.57735,0.57735,0.57735;2.0944rad)
  expr: Constraints[30] = <<Parameters>>.GlassOpeningHeigth
  expr: Constraints[31] = <<Parameters>>.MuntinTenonThickness
  expr: Constraints[32] = <<Parameters>>.GlassRebateDepth
  expr: Constraints[34] = <<Parameters>>.GlassOpeningHeigth + <<Parameters>>.RailBottomWidth
  expr: Constraints[35] = <<Parameters>>.GlassOpeningHeigth
  expr: Constraints[8] = <<Parameters>>.MuntinWidth
  sketch-geometry (12):
    g0: LineSegment StartX=-9.5 StartY=-290 StartZ=0 EndX=-9.5 EndY=-320 EndZ=0
    g1: LineSegment StartX=-9.5 StartY=-320 StartZ=0 EndX=0.5 EndY=-320 EndZ=0
    g2: LineSegment StartX=0.5 StartY=-320 StartZ=0 EndX=0.5 EndY=-290 EndZ=0
    g3: LineSegment StartX=0.5 StartY=-290 StartZ=0 EndX=-9.5 EndY=-290 EndZ=0
    g4: LineSegment StartX=-9.5 StartY=160 StartZ=0 EndX=-9.5 EndY=190 EndZ=0
    g5: LineSegment StartX=-9.5 StartY=190 StartZ=0 EndX=0.5 EndY=190 EndZ=0
    g6: LineSegment StartX=0.5 StartY=190 StartZ=0 EndX=0.5 EndY=160 EndZ=0
    g7: LineSegment StartX=0.5 StartY=160 StartZ=0 EndX=-9.5 EndY=160 EndZ=0
    g8: LineSegment StartX=-9.5 StartY=640 StartZ=0 EndX=-9.5 EndY=670 EndZ=0
    g9: LineSegment StartX=-9.5 StartY=670 StartZ=0 EndX=0.5 EndY=670 EndZ=0
    g10: LineSegment StartX=0.5 StartY=670 StartZ=0 EndX=0.5 EndY=640 EndZ=0
    g11: LineSegment StartX=0.5 StartY=640 StartZ=0 EndX=-9.5 EndY=640 EndZ=0
  constraints (36):
    c: Coincident(g0,g1)
    c: Coincident(g1,g2)
    c: Coincident(g2,g3)
    c: Coincident(g3,g0)
    c: Vertical(g0)
    c: Vertical(g2)
    c: Horizontal(g1)
    c: Horizontal(g3)
    c: DistanceY(g0,g0) = 30
    c: Coincident(g4,g5)
    c: Coincident(g8,g9)
    c: Coincident(g5,g6)
    c: Coincident(g9,g10)
    c: Coincident(g6,g7)
    c: Coincident(g10,g11)
    c: Coincident(g7,g4)
    c: Coincident(g11,g8)
    c: Vertical(g4)
    c: Vertical(g8)
    c: Vertical(g6)
    c: Vertical(g10)
    c: Horizontal(g5)
    c: Horizontal(g9)
    c: Horizontal(g7)
    c: Horizontal(g11)
    c: Equal(g0,g4)
    c: Equal(g0,g8)
    c: Equal(g11,g7)
    c: Equal(g7,g3)
    c: Vertical(g5,g9)
    c: DistanceY(g0,g4) = 450
    c: DistanceX(g1,g1) = 10
    c: Distance(g1,g-3) = 32
    c: Vertical(g9,g2)
    c: Distance(g0,g-4) = 615
    c: DistanceY(g4,g8) = 450
FEATURE [Sketcher::SketchObject] Sketch007  label="Frame rebate opening top002"
  ArcFitTolerance = 0
  AttachmentSupport = -> [DatumPlane004]
  ExternalGeometry = -> [DatumPlane003,DatumPlane005]
  FullyConstrained = true
  MakeInternals = false
  MapMode = 5
  Placement = pos=(45,0,0) rot=(0.57735,0.57735,0.57735;2.0944rad)
  expr: Constraints[6] = <<Parameters>>.WindowFrameRebateWidth
  expr: Constraints[7] = <<Parameters>>.WindowFrameRebateDepth
  sketch-geometry (4):
    g0: LineSegment StartX=12.5 StartY=935 StartZ=0 EndX=12.5 EndY=910 EndZ=0
    g1: LineSegment StartX=12.5 StartY=910 StartZ=0 EndX=32.5 EndY=910 EndZ=0
    g2: LineSegment StartX=32.5 StartY=910 StartZ=0 EndX=32.5 EndY=935 EndZ=0
    g3: LineSegment StartX=32.5 StartY=935 StartZ=0 EndX=12.5 EndY=935 EndZ=0
  constraints (10):
    c: Coincident(g0,g1)
    c: Coincident(g1,g2)
    c: Coincident(g2,g3)
    c: Coincident(g3,g0)
    c: Vertical(g0)
    c: Horizontal(g1)
    c: DistanceX(g3,g3) = 20
    c: Distance(g2,g2) = 25
    c: Tangent(g2,g-4)
    c: Tangent(g3,g-3)
FEATURE [Sketcher::SketchObject] Sketch008  label="Frame rebate closure top002"
  ArcFitTolerance = 0
  AttachmentSupport = -> [DatumPlane004]
  ExternalGeometry = -> [DatumPlane003,DatumPlane005]
  FullyConstrained = true
  MakeInternals = false
  MapMode = 5
  Placement = pos=(45,0,0) rot=(0.57735,0.57735,0.57735;2.0944rad)
  expr: Constraints[6] = <<Parameters>>.WindowInnerLipWidth
  expr: Constraints[7] = <<Parameters>>.FrameThickness
  sketch-geometry (4):
    g0: LineSegment StartX=-17.5 StartY=935 StartZ=0 EndX=-17.5 EndY=920 EndZ=0
    g1: LineSegment StartX=-17.5 StartY=920 StartZ=0 EndX=32.5 EndY=920 EndZ=0
    g2: LineSegment StartX=32.5 StartY=920 StartZ=0 EndX=32.5 EndY=935 EndZ=0
    g3: LineSegment StartX=32.5 StartY=935 StartZ=0 EndX=-17.5 EndY=935 EndZ=0
  constraints (10):
    c: Coincident(g0,g1)
    c: Coincident(g1,g2)
    c: Coincident(g2,g3)
    c: Coincident(g3,g0)
    c: Vertical(g0)
    c: Horizontal(g1)
    c: DistanceY(g2,g2) = 15
    c: DistanceX(g3,g3) = 50
    c: Tangent(g3,g-3)
    c: Tangent(g-4,g2)
FEATURE [PartDesign::Plane] DatumPlane007  label="DatumPlane left"
  AttachmentOffset = pos=(0,0,45) rot=(0,0,1;0rad)
  AttachmentSupport = -> [X_Axis001]
  Length = 65
  MapMode = 4
  Placement = pos=(-45,0,0) rot=(0.57735,-0.57735,-0.57735;2.0944rad)
  ResizeMode = 1
  Width = 1870
  expr: .AttachmentOffset.Base.z = <<Parameters>>.StileOuterWidth / 2
  expr: Length = <<Parameters>>.WindowThickness
  expr: Width = <<Parameters>>.StileLength
FEATURE [Sketcher::SketchObject] Sketch009  label="Frame rebate opening side002"
  ArcFitTolerance = 0
  AttachmentSupport = -> [DatumPlane003]
  ExternalGeometry = -> [DatumPlane005,DatumPlane007]
  FullyConstrained = true
  MakeInternals = false
  MapMode = 5
  Placement = pos=(0,0,935) rot=(0,0,1;0rad)
  expr: Constraints[6] = <<Parameters>>.WindowFrameRebateDepth
  expr: Constraints[7] = <<Parameters>>.WindowFrameRebateWidth
  sketch-geometry (4):
    g0: LineSegment StartX=-45 StartY=32.5 StartZ=0 EndX=-45 EndY=12.5 EndZ=0
    g1: LineSegment StartX=-45 StartY=12.5 StartZ=0 EndX=-20 EndY=12.5 EndZ=0
    g2: LineSegment StartX=-20 StartY=12.5 StartZ=0 EndX=-20 EndY=32.5 EndZ=0
    g3: LineSegment StartX=-20 StartY=32.5 StartZ=0 EndX=-45 EndY=32.5 EndZ=0
  constraints (10):
    c: Coincident(g0,g1)
    c: Coincident(g1,g2)
    c: Coincident(g2,g3)
    c: Coincident(g3,g0)
    c: Vertical(g2)
    c: Horizontal(g1)
    c: DistanceX(g3,g3) = 25
    c: DistanceY(g0,g0) = 20
    c: Tangent(g3,g-3)
    c: Tangent(g0,g-4)
FEATURE [Sketcher::SketchObject] Sketch010  label="Frame rebate closure right002"
  ArcFitTolerance = 0
  AttachmentSupport = -> [DatumPlane003]
  ExternalGeometry = -> [DatumPlane005,DatumPlane007]
  FullyConstrained = true
  MakeInternals = false
  MapMode = 5
  Placement = pos=(0,0,935) rot=(0,0,1;0rad)
  expr: Constraints[6] = <<Parameters>>.WindowInnerLipWidth
  expr: Constraints[7] = <<Parameters>>.FrameThickness
  sketch-geometry (4):
    g0: LineSegment StartX=-45 StartY=32.5 StartZ=0 EndX=-45 EndY=-17.5 EndZ=0
    g1: LineSegment StartX=-45 StartY=-17.5 StartZ=0 EndX=-30 EndY=-17.5 EndZ=0
    g2: LineSegment StartX=-30 StartY=-17.5 StartZ=0 EndX=-30 EndY=32.5 EndZ=0
    g3: LineSegment StartX=-30 StartY=32.5 StartZ=0 EndX=-45 EndY=32.5 EndZ=0
  constraints (10):
    c: Coincident(g0,g1)
    c: Coincident(g1,g2)
    c: Coincident(g2,g3)
    c: Coincident(g3,g0)
    c: Vertical(g2)
    c: Horizontal(g1)
    c: DistanceX(g3,g3) = 15
    c: DistanceY(g0,g0) = 50
    c: Tangent(g3,g-3)
    c: Tangent(g0,g-4)
FEATURE [Sketcher::SketchObject] Sketch019  label="Mortise rail top002"
  ArcFitTolerance = 0
  AttachmentOffset = pos=(0,0,-32) rot=(0,0,1;0rad)
  AttachmentSupport = -> [DatumPlane005]
  ExternalGeometry = -> [DatumPlane007,DatumPlane003]
  FullyConstrained = true
  MakeInternals = false
  MapMode = 5
  Placement = pos=(0,0.5,-1e-16) rot=(0,0.707107,0.707107;3.14159rad)
  expr: .AttachmentOffset.Base.z = -<<Parameters>>.GlassRebateDepth
  expr: Constraints[10] = <<Parameters>>.StileOuterWidth
  expr: Constraints[11] = <<Parameters>>.RailTopTenonWidth
  expr: Constraints[12] = <<Parameters>>.RailTopWidth
  expr: Constraints[13] = <<Parameters>>.StileOuterHaunchDepth
  sketch-geometry (6):
    g0: LineSegment StartX=-45 StartY=935 StartZ=0 EndX=-20 EndY=935 EndZ=0
    g1: LineSegment StartX=-20 StartY=935 StartZ=0 EndX=-20 EndY=890 EndZ=0
    g2: LineSegment StartX=-20 StartY=890 StartZ=0 EndX=45 EndY=890 EndZ=0
    g3: LineSegment StartX=45 StartY=890 StartZ=0 EndX=45 EndY=820 EndZ=0
    g4: LineSegment StartX=45 StartY=820 StartZ=0 EndX=-45 EndY=820 EndZ=0
    g5: LineSegment StartX=-45 StartY=820 StartZ=0 EndX=-45 EndY=935 EndZ=0
  constraints (16):
    c: Coincident(g0,g1)
    c: Vertical(g1)
    c: Coincident(g1,g2)
    c: Horizontal(g2)
    c: Coincident(g2,g3)
    c: Coincident(g3,g4)
    c: Horizontal(g4)
    c: Coincident(g4,g5)
    c: Coincident(g5,g0)
    c: Vertical(g5)
    c: DistanceX(g4,g4) = 90
    c: DistanceY(g3,g3) = 70
    c: DistanceY(g5,g5) = 115
    c: DistanceX(g0,g0) = 25
    c: Tangent(g-3,g3)
    c: Tangent(g0,g-4)
FEATURE [PartDesign::Pocket] Pocket016  label="Mortise rail top003"
  BaseFeature = -> Pad001
  Direction = (0,-1,2e-16)
  Length = 15
  Length2 = 5
  Placement = pos=(0,0,935) rot=(0,0,1;0rad)
  Profile = -> Sketch019
  ReferenceAxis = -> Sketch019 [N_Axis]
  Refine = true
  Suppressed = false
  Type = 0
  expr: Length = <<Parameters>>.RailTenonThickness
FEATURE [Sketcher::SketchObject] Sketch020
  ArcFitTolerance = 0
  AttachmentSupport = -> [DatumPlane003]
  ExternalGeometry = -> [DatumPlane005,DatumPlane004]
  FullyConstrained = true
  MakeInternals = false
  MapMode = 5
  Placement = pos=(0,0,935) rot=(0,0,1;0rad)
  expr: Constraints[6] = <<Parameters>>.GlassRebateDepth
  expr: Constraints[7] = <<Parameters>>.GlassRebateWidth
  sketch-geometry (4):
    g0: LineSegment StartX=35 StartY=32.5 StartZ=0 EndX=35 EndY=0.5 EndZ=0
    g1: LineSegment StartX=35 StartY=0.5 StartZ=0 EndX=45 EndY=0.5 EndZ=0
    g2: LineSegment StartX=45 StartY=0.5 StartZ=0 EndX=45 EndY=32.5 EndZ=0
    g3: LineSegment StartX=45 StartY=32.5 StartZ=0 EndX=35 EndY=32.5 EndZ=0
  constraints (10):
    c: Coincident(g0,g1)
    c: Coincident(g1,g2)
    c: Coincident(g2,g3)
    c: Coincident(g3,g0)
    c: Vertical(g0)
    c: Horizontal(g1)
    c: DistanceY(g2,g2) = 32
    c: DistanceX(g3,g3) = 10
    c: Tangent(g3,g-3)
    c: Tangent(g2,g-4)
FEATURE [Sketcher::SketchObject] Sketch021
  ArcFitTolerance = 0
  AttachmentOffset = pos=(0,0,-32) rot=(0,0,1;0rad)
  AttachmentSupport = -> [DatumPlane005]
  ExternalGeometry = -> [DatumPlane006,DatumPlane004]
  FullyConstrained = true
  MakeInternals = false
  MapMode = 5
  Placement = pos=(0,0.5,-1e-16) rot=(0,0.707107,0.707107;3.14159rad)
  expr: .AttachmentOffset.Base.z = -<<Parameters>>.GlassRebateDepth
  expr: Constraints[10] = <<Parameters>>.StileOuterWidth
  expr: Constraints[11] = <<Parameters>>.RailBottomTenonWidth
  expr: Constraints[12] = <<Parameters>>.RailBottomWidth
  expr: Constraints[13] = <<Parameters>>.StileOuterHaunchDepth
  sketch-geometry (6):
    g0: LineSegment StartX=45 StartY=-770 StartZ=0 EndX=-45 EndY=-770 EndZ=0
    g1: LineSegment StartX=-45 StartY=-770 StartZ=0 EndX=-45 EndY=-935 EndZ=0
    g2: LineSegment StartX=-45 StartY=-935 StartZ=0 EndX=-20 EndY=-935 EndZ=0
    g3: LineSegment StartX=-20 StartY=-935 StartZ=0 EndX=-20 EndY=-870 EndZ=0
    g4: LineSegment StartX=-20 StartY=-870 StartZ=0 EndX=45 EndY=-870 EndZ=0
    g5: LineSegment StartX=45 StartY=-870 StartZ=0 EndX=45 EndY=-770 EndZ=0
  constraints (16):
    c: Horizontal(g0)
    c: Coincident(g0,g1)
    c: Coincident(g1,g2)
    c: Coincident(g2,g3)
    c: Vertical(g3)
    c: Coincident(g3,g4)
    c: Horizontal(g4)
    c: Coincident(g4,g5)
    c: Coincident(g5,g0)
    c: Vertical(g5)
    c: DistanceX(g0,g0) = 90
    c: DistanceY(g5,g5) = 100
    c: DistanceY(g1,g1) = 165
    c: DistanceX(g2,g2) = 25
    c: Tangent(g2,g-3)
    c: Tangent(g1,g-4)
FEATURE [PartDesign::Pocket] Pocket018  label="Mortise rail bottom002"
  BaseFeature = -> Pocket016
  Direction = (0,-1,2e-16)
  Length = 15
  Length2 = 5
  Placement = pos=(0,0,935) rot=(0,0,1;0rad)
  Profile = -> Sketch021
  ReferenceAxis = -> Sketch021 [N_Axis]
  Refine = true
  Suppressed = false
  Type = 0
  expr: Length = <<Parameters>>.RailTenonThickness
FEATURE [PartDesign::Pocket] Pocket004  label="Mortises muntin"
  BaseFeature = -> Pocket018
  Direction = (-1,0,0)
  Length = 5
  Length2 = 5
  Placement = pos=(0,0,935) rot=(0,0,1;0rad)
  Profile = -> Sketch006
  ReferenceAxis = -> Sketch006 [N_Axis]
  Refine = true
  Suppressed = false
  Type = 1
FEATURE [PartDesign::Pocket] Pocket005  label="Frame rebate opening top"
  BaseFeature = -> Pocket004
  Direction = (-1,0,0)
  Length = 5
  Length2 = 5
  Placement = pos=(0,0,935) rot=(0,0,1;0rad)
  Profile = -> Sketch007
  ReferenceAxis = -> Sketch007 [N_Axis]
  Refine = true
  Suppressed = false
  Type = 1
FEATURE [PartDesign::Pocket] Pocket006  label="Frame rebate lip top"
  BaseFeature = -> Pocket005
  Direction = (-1,0,0)
  Length = 5
  Length2 = 5
  Placement = pos=(0,0,935) rot=(0,0,1;0rad)
  Profile = -> Sketch008
  ReferenceAxis = -> Sketch008 [N_Axis]
  Refine = true
  Suppressed = false
  Type = 1
FEATURE [PartDesign::Mirrored] Mirrored002  label="Frame rebates bottom"
  BaseFeature = -> Pocket006
  MirrorPlane = -> XY_Plane001
  Originals = -> [Pocket005,Pocket006]
  Placement = pos=(0,0,935) rot=(0,0,1;0rad)
  Refine = true
  Suppressed = false
  TransformMode = 0
FEATURE [PartDesign::Pocket] Pocket007  label="Frame rebate opening left"
  BaseFeature = -> Mirrored002
  Direction = (0,0,-1)
  Length = 5
  Length2 = 5
  Placement = pos=(0,0,935) rot=(0,0,1;0rad)
  Profile = -> Sketch009
  ReferenceAxis = -> Sketch009 [N_Axis]
  Refine = true
  Suppressed = false
  Type = 1
FEATURE [PartDesign::Pocket] Pocket008  label="Frame rebate lip left001"
  BaseFeature = -> Pocket007
  Direction = (0,0,-1)
  Length = 5
  Length2 = 5
  Placement = pos=(0,0,935) rot=(0,0,1;0rad)
  Profile = -> Sketch010
  ReferenceAxis = -> Sketch010 [N_Axis]
  Refine = true
  Suppressed = false
  Type = 1
FEATURE [PartDesign::Pocket] Pocket017  label="Glass rebate"
  BaseFeature = -> Pocket008
  Direction = (0,0,-1)
  Length = 5
  Length2 = 5
  Placement = pos=(0,0,935) rot=(0,0,1;0rad)
  Profile = -> Sketch020
  ReferenceAxis = -> Sketch020 [N_Axis]
  Refine = true
  Suppressed = false
  Type = 1
FEATURE [PartDesign::Body] Body001  label="Stile outer left"
  AllowCompound = false
  Group = -> [DatumPlane003,DatumPlane004,DatumPlane005,DatumPlane006,DatumPlane007,Sketch003,Pad001,Pocket016,Pocket018,Sketch006,Pocket004,Sketch007,Pocket005,Sketch008,Pocket006,Mirrored002,Sketch009,Sketch010,Pocket007,Pocket008,Sketch019,Sketch020,Pocket017,Sketch021]
  Origin = -> Origin001
  Tip = -> Pocket017
COMPONENT P16 — recipe-attached ("Stile outer right001", modeled in this document).
Construction recipe (the document's own serialized feature program — sketch geometry with constraints, then the solid features built on it; lengths are millimeters unless a unit is written):

FEATURE [PartDesign::FeatureBase] BaseFeature
  BaseFeature = -> Part__Mirroring
  Suppressed = false
FEATURE [PartDesign::Body] Body002  label="Stile outer right"
  AllowCompound = false
  BaseFeature = -> Part__Mirroring
  Group = -> [BaseFeature]
  Origin = -> Origin002
  Tip = -> BaseFeature
PROVENANCE & LICENSES
A FreeCAD (.FCStd) document from a public repository crawl; recipes are the document's own serialized feature recipes (and, for linked parts, companion documents' recipes).
License: lgpl-3.0.
